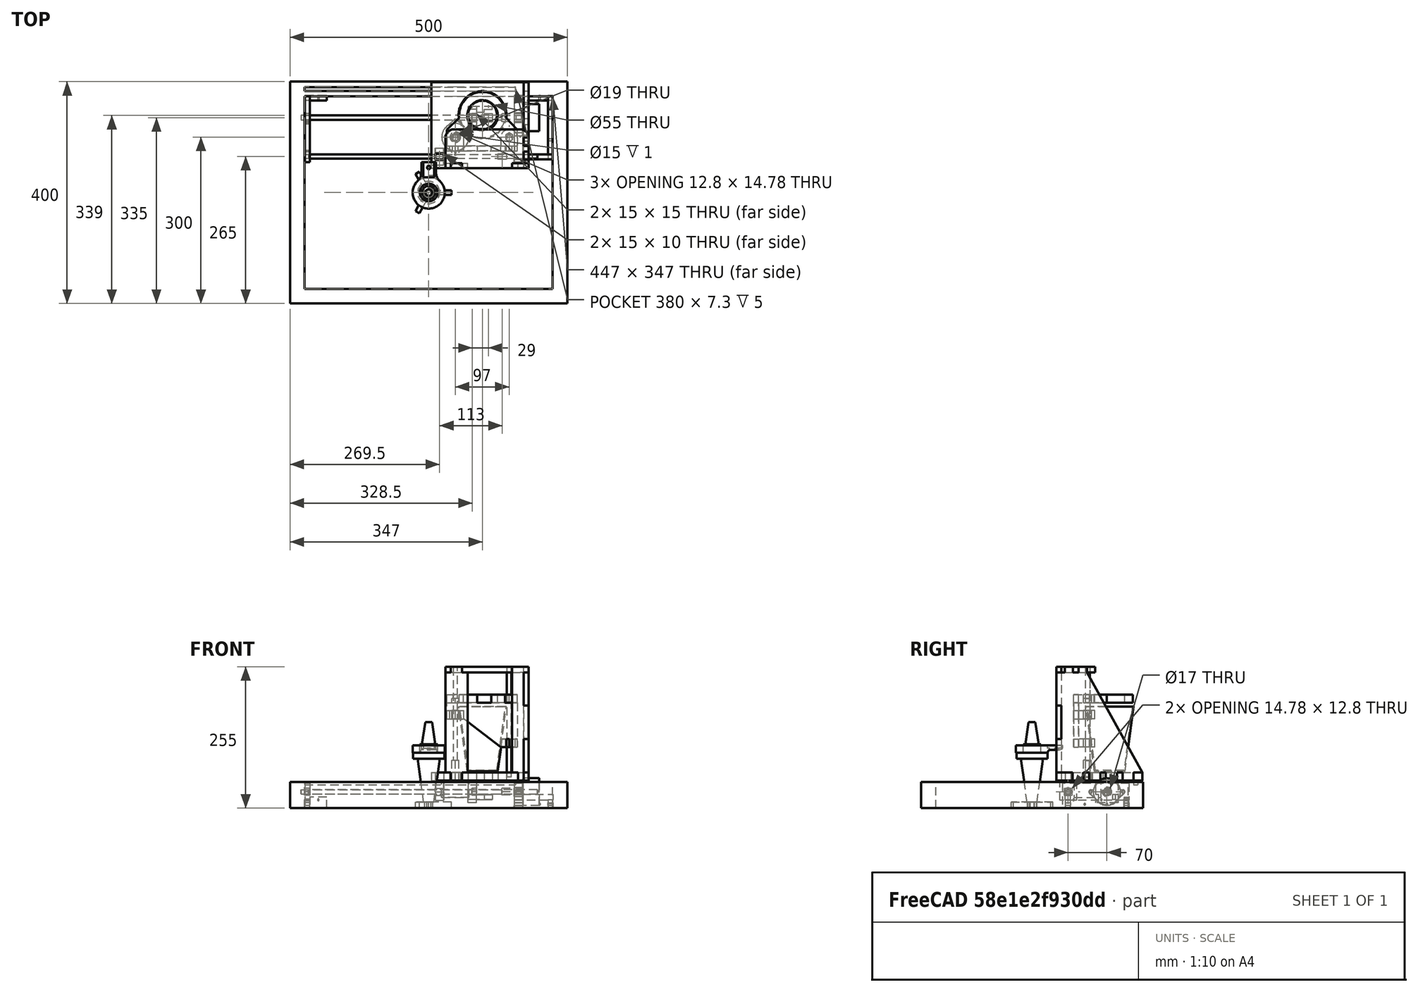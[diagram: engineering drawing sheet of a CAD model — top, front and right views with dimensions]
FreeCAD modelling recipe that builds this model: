
FCSTD DOCUMENT  (FreeCAD 0.19R19093 (Git))
Label: CocktailAutomat-neu
License: All rights reserved
LicenseURL: http://en.wikipedia.org/wiki/All_rights_reserved
objects: Sketcher::SketchObject×41, PartDesign::Body×32, PartDesign::Pad×32, PartDesign::ShapeBinder×14, PartDesign::Plane×7, PartDesign::CoordinateSystem×7, App::Part×7, TechDraw::DrawViewDimension×7, PartDesign::Pocket×6, PartDesign::Revolution×3, PartDesign::FeatureBase×3, TechDraw::DrawProjGroupItem×3, App::DocumentObjectGroup×2, PartDesign::Hole×1, TechDraw::DrawSVGTemplate×1, TechDraw::DrawProjGroup×1, App::FeaturePython×1, TechDraw::DrawPage×1
note: 188 computed .brp shape members not serialized (recipe doc carries the construction recipe); baked Part::Feature solids carry a one-line shape summary decoded from their .brp

FEATURE [Sketcher::SketchObject] Sketch
  MapMode = 5
  Placement = pos=(0,0,0) rot=(0.57735,0.57735,0.57735;2.0944rad)
  Support = -> [YZ_Plane]
  sketch-geometry (6):
    g0: LineSegment StartX=0 StartY=0 StartZ=0 EndX=27.5 EndY=0 EndZ=0
    g1: LineSegment StartX=27.5 StartY=0 StartZ=0 EndX=43 EndY=117 EndZ=0
    g2: LineSegment StartX=43 StartY=117 StartZ=0 EndX=40.9825 EndY=117 EndZ=0
    g3: LineSegment StartX=40.9825 StartY=117 StartZ=0 EndX=25.7475 EndY=2 EndZ=0
    g4: LineSegment StartX=25.7475 StartY=2 StartZ=0 EndX=0 EndY=2 EndZ=0
    g5: LineSegment StartX=0 StartY=2 StartZ=0 EndX=0 EndY=0 EndZ=0
  constraints (17):
    c: Coincident(g-1,g0)
    c: PointOnObject(g0,g-1)
    c: Coincident(g0,g1)
    c: Coincident(g1,g2)
    c: Coincident(g2,g3)
    c: Coincident(g3,g4)
    c: PointOnObject(g4,g-2)
    c: Horizontal(g4)
    c: Coincident(g4,g5)
    c: Coincident(g5,g0)
    c: DistanceX(g0,g0) = 27.5
    c: Parallel(g3,g1)
    c: DistanceY(g5,g5) = 2
    c: Horizontal(g2)
    c: Distance(g1,g-1) = 117
    c: Distance(g1,g-2) = 43
    c: Distance(g2,g1) = 2
FEATURE [PartDesign::Revolution] Revolution
  Angle = 360
  Axis = (-3e-16,3e-16,1)
  Base = (0,0,0)
  Placement = pos=(0,0,0) rot=(0.57735,0.57735,0.57735;2.0944rad)
  Profile = -> Sketch
  ReferenceAxis = -> Z_Axis
  Reversed = true
FEATURE [PartDesign::Body] Body  label="Glas"
  Group = -> [Sketch,Revolution]
  Origin = -> Origin
  Placement = pos=(97,140,66) rot=(0,0,1;0rad)
  Tip = -> Revolution
FEATURE [Sketcher::SketchObject] Sketch001
  MapMode = 5
  Support = -> [XY_Plane001]
  sketch-geometry (16):
    g0: Circle CenterX=0 CenterY=0 CenterZ=0 NormalX=0 NormalY=0 NormalZ=1 AngleXU=0 Radius=3.9
    g1: ArcOfCircle CenterX=0 CenterY=0 CenterZ=0 NormalX=0 NormalY=0 NormalZ=1 AngleXU=0 Radius=8.1 StartAngle=2.61088 EndAngle=3.6723
    g2: LineSegment StartX=7.04344 StartY=4 StartZ=0 EndX=41.0434 EndY=4 EndZ=0
    g3: LineSegment StartX=41.0434 StartY=4 StartZ=0 EndX=41.0434 EndY=-4 EndZ=0
    g4: LineSegment StartX=41.0434 StartY=-4 StartZ=0 EndX=7.04344 EndY=-4 EndZ=0
    g5: LineSegment StartX=-6.98582 StartY=4.0998 StartZ=0 EndX=-23.9858 EndY=33.5447 EndZ=0
    g6: LineSegment StartX=-23.9858 StartY=33.5447 StartZ=0 EndX=-17.0576 EndY=37.5447 EndZ=0
    g7: LineSegment StartX=-17.0576 StartY=37.5447 StartZ=0 EndX=-0.0576167 EndY=8.0998 EndZ=0
    g8: LineSegment StartX=-6.98582 StartY=-4.0998 StartZ=0 EndX=-23.9858 EndY=-33.5447 EndZ=0
    g9: LineSegment StartX=-23.9858 StartY=-33.5447 StartZ=0 EndX=-17.0576 EndY=-37.5447 EndZ=0
    g10: LineSegment StartX=-17.0576 StartY=-37.5447 StartZ=0 EndX=-0.0576167 EndY=-8.0998 EndZ=0
    g11: LineSegment [constr] StartX=0 StartY=0 StartZ=0 EndX=41.0434 EndY=0 EndZ=0
    g12: LineSegment [constr] StartX=0 StartY=0 StartZ=0 EndX=-20.5217 EndY=35.5447 EndZ=0
    g13: LineSegment [constr] StartX=0 StartY=0 StartZ=0 EndX=-20.5217 EndY=-35.5447 EndZ=0
    g14: ArcOfCircle CenterX=0 CenterY=0 CenterZ=0 NormalX=0 NormalY=0 NormalZ=1 AngleXU=0 Radius=8.1 StartAngle=0.516486 EndAngle=1.57791
    g15: ArcOfCircle CenterX=0 CenterY=0 CenterZ=0 NormalX=0 NormalY=0 NormalZ=1 AngleXU=0 Radius=8.1 StartAngle=4.70528 EndAngle=5.7667
  constraints (44):
    c: Coincident(g1,g0)
    c: Coincident(g2,g3)
    c: Coincident(g3,g4)
    c: Coincident(g5,g6)
    c: Coincident(g6,g7)
    c: Coincident(g8,g9)
    c: Coincident(g9,g10)
    c: Coincident(g11,g0)
    c: PointOnObject(g11,g3)
    c: Coincident(g12,g0)
    c: PointOnObject(g12,g6)
    c: Coincident(g13,g0)
    c: PointOnObject(g13,g9)
    c: Diameter(g0) = 7.8
    c: Diameter(g1) = 16.2
    c: Angle(g11,g12) = 2.0944
    c: Angle(g13,g11) = 2.0944
    c: Symmetric(g5,g6,g12)
    c: Distance(g6) = 8
    c: Symmetric(g8,g9,g13)
    c: Parallel(g5,g7)
    c: Parallel(g5,g12)
    c: Parallel(g8,g13)
    c: Parallel(g13,g10)
    c: Distance(g9) = 8
    c: Symmetric(g3,g2,g11)
    c: Parallel(g2,g11)
    c: Parallel(g11,g4)
    c: Distance(g3) = 8
    c: Coincident(g-1,g0)
    c: Horizontal(g11)
    c: Coincident(g1,g5)
    c: Coincident(g14,g7)
    c: Equal(g1,g14)
    c: Coincident(g14,g2)
    c: Coincident(g1,g14)
    c: Coincident(g15,g4)
    c: Equal(g1,g15)
    c: Coincident(g15,g10)
    c: Coincident(g1,g15)
    c: Coincident(g1,g8)
    c: DistanceX(g2,g2) = 34
    c: Distance(g7) = 34
    c: Distance(g8) = 34
FEATURE [PartDesign::Pad] Pad
  Length = 11
  Length2 = 100
  Profile = -> Sketch001
  Type = 0
FEATURE [PartDesign::Body] Body001  label="Dosierer-unten"
  Group = -> [Sketch001,Pad]
  Origin = -> Origin001
  Tip = -> Pad
FEATURE [Sketcher::SketchObject] Sketch002
  MapMode = 5
  Placement = pos=(0,0,0) rot=(0.57735,0.57735,0.57735;2.0944rad)
  Support = -> [YZ_Plane002]
  sketch-geometry (14):
    g0: LineSegment StartX=0 StartY=11 StartZ=0 EndX=9 EndY=11 EndZ=0
    g1: LineSegment StartX=9 StartY=11 StartZ=0 EndX=20 EndY=89 EndZ=0
    g2: LineSegment StartX=20 StartY=89 StartZ=0 EndX=28 EndY=89 EndZ=0
    g3: LineSegment StartX=28 StartY=89 StartZ=0 EndX=28 EndY=100 EndZ=0
    g4: LineSegment StartX=16 StartY=100 StartZ=0 EndX=16 EndY=115 EndZ=0
    g5: LineSegment StartX=16 StartY=115 StartZ=0 EndX=12 EndY=115 EndZ=0
    g6: LineSegment StartX=12 StartY=115 StartZ=0 EndX=6 EndY=155 EndZ=0
    g7: LineSegment StartX=6 StartY=155 StartZ=0 EndX=0 EndY=155 EndZ=0
    g8: LineSegment StartX=0 StartY=155 StartZ=0 EndX=0 EndY=11 EndZ=0
    g9: LineSegment [constr] StartX=6 StartY=155 StartZ=0 EndX=12 EndY=155 EndZ=0
    g10: LineSegment [constr] StartX=12 StartY=115 StartZ=0 EndX=12 EndY=155 EndZ=0
    g11: LineSegment [constr] StartX=9 StartY=11 StartZ=0 EndX=20 EndY=11 EndZ=0
    g12: LineSegment [constr] StartX=20 StartY=89 StartZ=0 EndX=20 EndY=11 EndZ=0
    g13: LineSegment StartX=16 StartY=100 StartZ=0 EndX=28 EndY=100 EndZ=0
  constraints (42):
    c: PointOnObject(g0,g-2)
    c: Horizontal(g0)
    c: Coincident(g1,g2)
    c: Coincident(g2,g3)
    c: Vertical(g3)
    c: Vertical(g4)
    c: Coincident(g4,g5)
    c: Coincident(g5,g6)
    c: Coincident(g6,g7)
    c: PointOnObject(g7,g-2)
    c: Coincident(g8,g7)
    c: Coincident(g8,g0)
    c: Distance(g0) = 9
    c: Coincident(g1,g0)
    c: Distance(g1,g8) = 20
    c: Distance(g3) = 11
    c: Perpendicular(g2,g3)
    c: Distance(g2) = 8
    c: Distance(g4) = 15
    c: Distance(g5) = 4
    c: Perpendicular(g4,g5)
    c: Distance(g7) = 6
    c: Horizontal(g7)
    c: Coincident(g9,g6)
    c: Horizontal(g9)
    c: Coincident(g10,g5)
    c: Coincident(g10,g9)
    c: Vertical(g10)
    c: Distance(g10) = 40
    c: Coincident(g11,g0)
    c: Coincident(g12,g1)
    c: Coincident(g12,g11)
    c: Vertical(g12)
    c: Horizontal(g11)
    c: Distance(g12) = 78
    c: Distance(g0,g-1) = 11
    c: Coincident(g13,g4)
    c: Coincident(g13,g3)
    c: Horizontal(g13)
    c: Distance(g13) = 12
    c: Distance(g3,g-1) = 100
    c: Distance(g3,g8) = 28
FEATURE [PartDesign::Revolution] Revolution001
  Angle = 360
  Axis = (-3e-16,3e-16,1)
  Base = (0,0,0)
  Placement = pos=(0,0,0) rot=(0.57735,0.57735,0.57735;2.0944rad)
  Profile = -> Sketch002
  ReferenceAxis = -> Z_Axis002
  Reversed = true
FEATURE [PartDesign::Body] Body002  label="Dosierer - mitte"
  Group = -> [Sketch002,Revolution001]
  Origin = -> Origin002
  Tip = -> Revolution001
FEATURE [PartDesign::ShapeBinder] CopyRevolution001
  Placement = pos=(0,0,0) rot=(0.57735,0.57735,0.57735;2.0944rad)
  TraceSupport = false
FEATURE [PartDesign::Plane] DatumPlane
  Length = 97.9587
  MapMode = 5
  Placement = pos=(-5.6e-14,3.3e-14,100) rot=(0,0,-1;1.5708rad)
  ResizeMode = 0
  Support = -> [CopyRevolution001]
  Width = 71.948
FEATURE [Sketcher::SketchObject] Sketch003
  MapMode = 5
  Placement = pos=(-5.6e-14,3.3e-14,100) rot=(0,0,-1;1.5708rad)
  Support = -> [CopyRevolution001]
  sketch-geometry (6):
    g0: LineSegment StartX=-55 StartY=-13 StartZ=0 EndX=-55 EndY=13 EndZ=0
    g1: LineSegment StartX=-55 StartY=13 StartZ=0 EndX=-37 EndY=13 EndZ=0
    g2: LineSegment StartX=-37 StartY=-13 StartZ=0 EndX=-55 EndY=-13 EndZ=0
    g3: ArcOfCircle CenterX=0 CenterY=0 CenterZ=0 NormalX=0 NormalY=0 NormalZ=1 AngleXU=0 Radius=29 StartAngle=3.89609 EndAngle=8.67028
    g4: ArcOfCircle CenterX=-37 CenterY=34.7813 CenterZ=0 NormalX=0 NormalY=0 NormalZ=1 AngleXU=0 Radius=21.7813 StartAngle=4.71239 EndAngle=5.52869
    g5: ArcOfCircle CenterX=-37 CenterY=-34.7812 CenterZ=0 NormalX=0 NormalY=0 NormalZ=1 AngleXU=0 Radius=21.7812 StartAngle=0.754498 EndAngle=1.5708
  constraints (15):
    c: Coincident(g0,g1)
    c: Horizontal(g1)
    c: Coincident(g2,g0)
    c: Symmetric(g0,g0,g-1)
    c: Distance(g0) = 26
    c: Coincident(g3,g-1)
    c: Diameter(g3) = 58
    c: Horizontal(g2)
    c: Distance(g3,g0) = 55
    c: Tangent(g1,g4) = -1.5708
    c: Tangent(g3,g4) = 1.5708
    c: Tangent(g2,g5) = -1.5708
    c: Tangent(g3,g5) = 1.5708
    c: Distance(g1) = 18
    c: Equal(g2,g1)
FEATURE [PartDesign::Pad] Pad001
  Length = 13
  Length2 = 100
  Placement = pos=(0,0,0) rot=(0.57735,0.57735,0.57735;2.0944rad)
  Profile = -> Sketch003
  Type = 0
FEATURE [Sketcher::SketchObject] Sketch004
  ExternalGeometry = -> [Pad001]
  MapMode = 5
  Placement = pos=(-4.41e-14,3.96e-14,113) rot=(0,0,-1;1.5708rad)
  Support = -> [Pad001]
  sketch-geometry (4):
    g0: LineSegment StartX=-55 StartY=10 StartZ=0 EndX=-27.5 EndY=10 EndZ=0
    g1: LineSegment StartX=-27.5 StartY=10 StartZ=0 EndX=-27.5 EndY=-10 EndZ=0
    g2: LineSegment StartX=-27.5 StartY=-10 StartZ=0 EndX=-55 EndY=-10 EndZ=0
    g3: LineSegment StartX=-55 StartY=-10 StartZ=0 EndX=-55 EndY=10 EndZ=0
  constraints (11):
    c: Coincident(g0,g1)
    c: Coincident(g1,g2)
    c: Coincident(g2,g3)
    c: Coincident(g3,g0)
    c: Horizontal(g0)
    c: Horizontal(g2)
    c: Vertical(g1)
    c: PointOnObject(g0,g-3)
    c: Symmetric(g2,g0,g-1)
    c: Distance(g3) = 20
    c: Distance(g0) = 27.5
FEATURE [PartDesign::Pocket] Pocket
  BaseFeature = -> Pad001
  Length = 4.5
  Length2 = 100
  Placement = pos=(0,0,0) rot=(0.57735,0.57735,0.57735;2.0944rad)
  Profile = -> Sketch004
  Type = 0
FEATURE [Sketcher::SketchObject] Sketch005
  ExternalGeometry = -> [Pocket]
  MapMode = 5
  Placement = pos=(-7.7e-14,5.64e-14,108.5) rot=(0,0,-1;1.5708rad)
  Support = -> [Pocket]
  sketch-geometry (1):
    g0: Circle CenterX=-45.05 CenterY=0 CenterZ=0 NormalX=0 NormalY=0 NormalZ=1 AngleXU=0 Radius=2.45
  constraints (3):
    c: PointOnObject(g0,g-1)
    c: Diameter(g0) = 4.9
    c: Distance(g0,g-3) = 9.95
FEATURE [PartDesign::Hole] Hole
  BaseFeature = -> Pocket
  Depth = 25
  DepthType = 0
  Diameter = 6
  DrillPoint = 1
  DrillPointAngle = 118
  HoleCutCountersinkAngle = 90
  HoleCutDepth = 0
  HoleCutDiameter = 0
  HoleCutType = 0
  ModelActualThread = false
  Placement = pos=(0,0,0) rot=(0.57735,0.57735,0.57735;2.0944rad)
  Profile = -> Sketch005
  Tapered = false
  TaperedAngle = 90
  ThreadAngle = 0
  ThreadClass = 0
  ThreadCutOffInner = 0
  ThreadCutOffOuter = 0
  ThreadDirection = 0
  ThreadFit = 0
  ThreadPitch = 0
  ThreadSize = 0
  ThreadType = 0
  Threaded = false
FEATURE [Sketcher::SketchObject] Sketch006
  ExternalGeometry = -> [Hole]
  MapMode = 5
  Placement = pos=(13,2.9e-15,1.01e-14) rot=(0.57735,0.57735,0.57735;2.0944rad)
  Support = -> [Hole]
  sketch-geometry (5):
    g0: LineSegment StartX=55 StartY=107 StartZ=0 EndX=49 EndY=105 EndZ=0
    g1: LineSegment StartX=49 StartY=105 StartZ=0 EndX=30.5 EndY=105 EndZ=0
    g2: LineSegment StartX=30.5 StartY=105 StartZ=0 EndX=27.5 EndY=100 EndZ=0
    g3: LineSegment StartX=27.5 StartY=100 StartZ=0 EndX=55 EndY=100 EndZ=0
    g4: LineSegment StartX=55 StartY=100 StartZ=0 EndX=55 EndY=107 EndZ=0
  constraints (14):
    c: Coincident(g0,g1)
    c: Horizontal(g1)
    c: Coincident(g1,g2)
    c: Coincident(g2,g3)
    c: Horizontal(g3)
    c: Coincident(g3,g4)
    c: Coincident(g4,g0)
    c: Vertical(g4)
    c: Coincident(g3,g-3)
    c: Distance(g0,g-3) = 6
    c: DistanceY(g1,g-3) = 8
    c: Distance(g3) = 27.5
    c: Distance(g1) = 18.5
    c: Distance(g0,g4) = 6
FEATURE [PartDesign::Pocket] Pocket001
  BaseFeature = -> Hole
  Length = 27
  Length2 = 100
  Midplane = true
  Placement = pos=(0,0,0) rot=(0.57735,0.57735,0.57735;2.0944rad)
  Profile = -> Sketch006
  Type = 1
FEATURE [PartDesign::Body] Body003  label="Dosierer halterung"
  Group = -> [DatumPlane,CopyRevolution001,Sketch003,Pad001,Sketch004,Pocket,Sketch005,Hole,Sketch006,Pocket001]
  Origin = -> Origin003
  Tip = -> Pocket001
FEATURE [Sketcher::SketchObject] Sketch007
  MapMode = 5
  Support = -> [XY_Plane004]
  sketch-geometry (8):
    g0: LineSegment StartX=-223.5 StartY=173.5 StartZ=0 EndX=223.5 EndY=173.5 EndZ=0
    g1: LineSegment StartX=223.5 StartY=173.5 StartZ=0 EndX=223.5 EndY=-173.5 EndZ=0
    g2: LineSegment StartX=223.5 StartY=-173.5 StartZ=0 EndX=-223.5 EndY=-173.5 EndZ=0
    g3: LineSegment StartX=-223.5 StartY=-173.5 StartZ=0 EndX=-223.5 EndY=173.5 EndZ=0
    g4: LineSegment StartX=-250 StartY=200 StartZ=0 EndX=250 EndY=200 EndZ=0
    g5: LineSegment StartX=250 StartY=200 StartZ=0 EndX=250 EndY=-200 EndZ=0
    g6: LineSegment StartX=250 StartY=-200 StartZ=0 EndX=-250 EndY=-200 EndZ=0
    g7: LineSegment StartX=-250 StartY=-200 StartZ=0 EndX=-250 EndY=200 EndZ=0
  constraints (20):
    c: Coincident(g0,g1)
    c: Coincident(g1,g2)
    c: Coincident(g2,g3)
    c: Coincident(g3,g0)
    c: Horizontal(g2)
    c: Vertical(g3)
    c: Coincident(g4,g5)
    c: Coincident(g5,g6)
    c: Coincident(g6,g7)
    c: Coincident(g7,g4)
    c: Horizontal(g6)
    c: Vertical(g7)
    c: DistanceY(g5,g5) = 400
    c: DistanceX(g4,g4) = 500
    c: Distance(g1,g5) = 26.5
    c: Symmetric(g4,g4,g-2)
    c: Symmetric(g0,g0,g-2)
    c: Symmetric(g4,g5,g-1)
    c: Distance(g1,g6) = 26.5
    c: Symmetric(g0,g1,g-1)
FEATURE [PartDesign::Pad] Pad002
  Length = 47
  Length2 = 100
  Profile = -> Sketch007
  Type = 0
FEATURE [Sketcher::SketchObject] Sketch008
  ExternalGeometry = -> [Pad002]
  MapMode = 5
  Placement = pos=(-223.5,0,0) rot=(0.57735,0.57735,0.57735;2.0944rad)
  Support = -> [Pad002]
  sketch-geometry (8):
    g0: LineSegment StartX=183.1 StartY=42 StartZ=0 EndX=183.1 EndY=47 EndZ=0
    g1: LineSegment StartX=183.1 StartY=47 StartZ=0 EndX=190.4 EndY=47 EndZ=0
    g2: LineSegment StartX=190.4 StartY=47 StartZ=0 EndX=190.4 EndY=42 EndZ=0
    g3: LineSegment StartX=190.4 StartY=42 StartZ=0 EndX=189.4 EndY=42 EndZ=0
    g4: LineSegment StartX=189.4 StartY=42 StartZ=0 EndX=189.4 EndY=46 EndZ=0
    g5: LineSegment StartX=189.4 StartY=46 StartZ=0 EndX=184.1 EndY=46 EndZ=0
    g6: LineSegment StartX=184.1 StartY=46 StartZ=0 EndX=184.1 EndY=42 EndZ=0
    g7: LineSegment StartX=184.1 StartY=42 StartZ=0 EndX=183.1 EndY=42 EndZ=0
  constraints (24):
    c: Vertical(g0)
    c: Coincident(g0,g1)
    c: Coincident(g1,g2)
    c: Coincident(g2,g3)
    c: Coincident(g3,g4)
    c: Coincident(g4,g5)
    c: Coincident(g5,g6)
    c: Coincident(g6,g7)
    c: Coincident(g7,g0)
    c: Vertical(g2)
    c: Horizontal(g1)
    c: Horizontal(g5)
    c: Horizontal(g7)
    c: Horizontal(g3)
    c: Vertical(g6)
    c: Vertical(g4)
    c: DistanceX(g1,g1) = 7.3
    c: Distance(g4,g2) = 1
    c: DistanceY(g0,g0) = 5
    c: Distance(g5,g0) = 1
    c: DistanceY(g2,g2) = 5
    c: Distance(g5,g1) = 1
    c: DistanceX(g-3,g0) = 9.6
    c: DistanceY(g0,g-3) = 0
FEATURE [PartDesign::Pad] Pad003
  BaseFeature = -> Pad002
  Length = 380
  Length2 = 100
  Profile = -> Sketch008
  Type = 0
FEATURE [PartDesign::Pocket] Pocket002
  BaseFeature = -> Pad003
  Length = 5
  Length2 = 100
  Profile = -> Pad003 [Face11]
  Type = 0
FEATURE [PartDesign::Body] Body004  label="Grundgestell"
  Group = -> [Sketch007,Pad002,Sketch008,Pad003,Pocket002]
  Origin = -> Origin004
  Tip = -> Pocket002
FEATURE [Sketcher::SketchObject] Sketch009
  MapMode = 5
  Placement = pos=(0,0,0) rot=(0.57735,0.57735,0.57735;2.0944rad)
  Support = -> [YZ_Plane005]
  sketch-geometry (1):
    g0: Circle CenterX=0 CenterY=0 CenterZ=0 NormalX=0 NormalY=0 NormalZ=1 AngleXU=0 Radius=24.5
  constraints (2):
    c: Diameter(g0) = 49
    c: Coincident(g0,g-1)
FEATURE [PartDesign::Pad] Pad004
  Length = 29
  Length2 = 100
  Placement = pos=(0,0,0) rot=(0.57735,0.57735,0.57735;2.0944rad)
  Profile = -> Sketch009
  Type = 0
FEATURE [Sketcher::SketchObject] Sketch010
  MapMode = 5
  Support = -> [XY_Plane005]
  sketch-geometry (8):
    g0: LineSegment StartX=-2 StartY=5 StartZ=0 EndX=-2 EndY=2 EndZ=0
    g1: LineSegment StartX=-2 StartY=2 StartZ=0 EndX=-3 EndY=2 EndZ=0
    g2: LineSegment StartX=-3 StartY=2 StartZ=0 EndX=-3 EndY=3.8 EndZ=0
    g3: LineSegment StartX=-3 StartY=3.8 StartZ=0 EndX=-13 EndY=3.8 EndZ=0
    g4: LineSegment StartX=-13 StartY=3.8 StartZ=0 EndX=-13 EndY=0 EndZ=0
    g5: LineSegment StartX=-13 StartY=0 StartZ=0 EndX=0 EndY=0 EndZ=0
    g6: LineSegment StartX=0 StartY=0 StartZ=0 EndX=0 EndY=5 EndZ=0
    g7: LineSegment StartX=-2 StartY=5 StartZ=0 EndX=0 EndY=5 EndZ=0
  constraints (23):
    c: Coincident(g0,g1)
    c: Coincident(g1,g2)
    c: Coincident(g2,g3)
    c: Horizontal(g3)
    c: Coincident(g3,g4)
    c: PointOnObject(g4,g-1)
    c: Vertical(g4)
    c: Coincident(g4,g5)
    c: Coincident(g5,g-1)
    c: Coincident(g5,g6)
    c: Vertical(g6)
    c: Coincident(g7,g0)
    c: Coincident(g7,g6)
    c: Horizontal(g7)
    c: Vertical(g0)
    c: Horizontal(g1)
    c: Vertical(g2)
    c: DistanceY(g6,g6) = 5
    c: DistanceX(g7,g7) = 2
    c: DistanceY(g0,g0) = 3
    c: DistanceX(g1,g1) = 1
    c: DistanceX(g3,g3) = 10
    c: DistanceY(g4,g4) = 3.8
FEATURE [PartDesign::Revolution] Revolution002
  Angle = 360
  Axis = (1,0,0)
  Base = (0,0,0)
  BaseFeature = -> Pad004
  Placement = pos=(0,0,0) rot=(0.57735,0.57735,0.57735;2.0944rad)
  Profile = -> Sketch010
  ReferenceAxis = -> X_Axis005
FEATURE [Sketcher::SketchObject] Sketch011
  MapMode = 5
  Placement = pos=(0,0,0) rot=(0.57735,0.57735,0.57735;2.0944rad)
  Support = -> [YZ_Plane005]
  sketch-geometry (11):
    g0: Circle [constr] CenterX=0 CenterY=0 CenterZ=0 NormalX=0 NormalY=0 NormalZ=1 AngleXU=0 Radius=23.25
    g1: ArcOfCircle CenterX=-29 CenterY=0 CenterZ=0 NormalX=0 NormalY=0 NormalZ=1 AngleXU=0 Radius=3.5 StartAngle=1.5708 EndAngle=3.96321
    g2: ArcOfCircle CenterX=29 CenterY=0 CenterZ=0 NormalX=0 NormalY=0 NormalZ=1 AngleXU=0 Radius=3.5 StartAngle=5.46156 EndAngle=7.85398
    g3: LineSegment StartX=31.3836 StartY=-2.56288 StartZ=0 EndX=15.8341 EndY=-17.0248 EndZ=0
    g4: LineSegment StartX=22.985 StartY=3.5 StartZ=0 EndX=29 EndY=3.5 EndZ=0
    g5: LineSegment StartX=-31.3836 StartY=-2.56288 StartZ=0 EndX=-15.834 EndY=-17.0248 EndZ=0
    g6: LineSegment StartX=-29 StartY=3.5 StartZ=0 EndX=-22.985 EndY=3.5 EndZ=0
    g7: ArcOfCircle CenterX=0 CenterY=0 CenterZ=0 NormalX=0 NormalY=0 NormalZ=1 AngleXU=0 Radius=23.25 StartAngle=0.151112 EndAngle=2.99048
    g8: ArcOfCircle CenterX=0 CenterY=0 CenterZ=0 NormalX=0 NormalY=0 NormalZ=1 AngleXU=0 Radius=23.25 StartAngle=3.96321 EndAngle=5.46156
    g9: Circle CenterX=-29 CenterY=0 CenterZ=0 NormalX=0 NormalY=0 NormalZ=1 AngleXU=0 Radius=2.5
    g10: Circle CenterX=29 CenterY=0 CenterZ=0 NormalX=0 NormalY=0 NormalZ=1 AngleXU=0 Radius=2.5
  constraints (30):
    c: Diameter(g0) = 46.5
    c: PointOnObject(g1,g-1)
    c: Symmetric(g1,g2,g-2)
    c: Equal(g2,g1)
    c: Diameter(g2) = 7
    c: DistanceX(g-2,g2) = 29
    c: Coincident(g0,g-1)
    c: Tangent(g3,g0)
    c: Tangent(g3,g2)
    c: PointOnObject(g4,g0)
    c: Horizontal(g4)
    c: PointOnObject(g5,g0)
    c: Horizontal(g6)
    c: Tangent(g6,g1)
    c: Tangent(g5,g0)
    c: Coincident(g7,g-1)
    c: Coincident(g7,g4)
    c: Coincident(g7,g6)
    c: Coincident(g8,g7)
    c: Coincident(g8,g5)
    c: Coincident(g8,g3)
    c: Tangent(g4,g2)
    c: Coincident(g1,g6)
    c: Coincident(g2,g3)
    c: Coincident(g2,g4)
    c: Tangent(g1,g5) = -1.5708
    c: Coincident(g9,g1)
    c: Coincident(g10,g2)
    c: Equal(g10,g9)
    c: Diameter(g9) = 5
FEATURE [PartDesign::Pad] Pad005
  BaseFeature = -> Revolution002
  Length = 0.8
  Length2 = 100
  Placement = pos=(0,0,0) rot=(0.57735,0.57735,0.57735;2.0944rad)
  Profile = -> Sketch011
  Reversed = true
  Type = 0
FEATURE [PartDesign::Body] Body005  label="Motor"
  Group = -> [Sketch009,Pad004,Sketch010,Revolution002,Sketch011,Pad005]
  Origin = -> Origin005
  Placement = pos=(170,135,29.5) rot=(0,0,1;0rad)
  Tip = -> Pad005
FEATURE [Sketcher::SketchObject] Sketch012
  MapMode = 5
  Placement = pos=(0,0,0) rot=(0.57735,0.57735,0.57735;2.0944rad)
  Support = -> [YZ_Plane007]
  sketch-geometry (1):
    g0: Circle CenterX=0 CenterY=0 CenterZ=0 NormalX=0 NormalY=0 NormalZ=1 AngleXU=0 Radius=4
  constraints (2):
    c: Coincident(g0,g-1)
    c: Diameter(g0) = 8
FEATURE [PartDesign::Pad] Pad006
  Length = 413
  Length2 = 100
  Placement = pos=(0,0,0) rot=(0.57735,0.57735,0.57735;2.0944rad)
  Profile = -> Sketch012
  Type = 0
FEATURE [PartDesign::Body] Body007  label="runde Stange"
  Group = -> [Sketch012,Pad006]
  Origin = -> Origin007
  Placement = pos=(-217,65,29) rot=(0,0,1;0rad)
  Tip = -> Pad006
FEATURE [Sketcher::SketchObject] Sketch033
  MapMode = 5
  Support = -> [XY_Plane012]
  sketch-geometry (1):
    g0: Circle CenterX=0 CenterY=0 CenterZ=0 NormalX=0 NormalY=0 NormalZ=1 AngleXU=0 Radius=24.5
  constraints (2):
    c: Coincident(g0,g-1)
    c: Diameter(g0) = 49
FEATURE [PartDesign::Pad] Pad011
  Length = 29
  Length2 = 100
  Profile = -> Sketch033
  Reversed = true
  Type = 0
FEATURE [Sketcher::SketchObject] Sketch034
  MapMode = 5
  Support = -> [Pad011]
  sketch-geometry (14):
    g0: Circle CenterX=0 CenterY=0 CenterZ=0 NormalX=0 NormalY=0 NormalZ=1 AngleXU=0 Radius=7.5
    g1: Circle CenterX=-28.2 CenterY=0 CenterZ=0 NormalX=0 NormalY=0 NormalZ=1 AngleXU=0 Radius=1.5
    g2: Circle CenterX=28.2 CenterY=0 CenterZ=0 NormalX=0 NormalY=0 NormalZ=1 AngleXU=0 Radius=1.5
    g3: Circle [constr] CenterX=0 CenterY=0 CenterZ=0 NormalX=0 NormalY=0 NormalZ=1 AngleXU=0 Radius=24.5
    g4: Circle [constr] CenterX=-28.2 CenterY=0 CenterZ=0 NormalX=0 NormalY=0 NormalZ=1 AngleXU=0 Radius=4
    g5: Circle [constr] CenterX=28.2 CenterY=0 CenterZ=0 NormalX=0 NormalY=0 NormalZ=1 AngleXU=0 Radius=4
    g6: LineSegment StartX=-31.1078 StartY=2.74676 StartZ=0 EndX=-17.8103 EndY=16.8239 EndZ=0
    g7: LineSegment StartX=17.8103 StartY=16.8239 StartZ=0 EndX=31.1078 EndY=2.74676 EndZ=0
    g8: LineSegment StartX=-31.1078 StartY=-2.74676 StartZ=0 EndX=-17.8103 EndY=-16.8239 EndZ=0
    g9: LineSegment StartX=17.8103 StartY=-16.8239 StartZ=0 EndX=31.1078 EndY=-2.74676 EndZ=0
    g10: ArcOfCircle CenterX=-28.2 CenterY=0 CenterZ=0 NormalX=0 NormalY=0 NormalZ=1 AngleXU=0 Radius=4 StartAngle=2.38467 EndAngle=3.89852
    g11: ArcOfCircle CenterX=0 CenterY=0 CenterZ=0 NormalX=0 NormalY=0 NormalZ=1 AngleXU=0 Radius=24.5 StartAngle=3.89852 EndAngle=5.52626
    g12: ArcOfCircle CenterX=0 CenterY=0 CenterZ=0 NormalX=0 NormalY=0 NormalZ=1 AngleXU=0 Radius=24.5 StartAngle=0.756926 EndAngle=2.38467
    g13: ArcOfCircle CenterX=28.2 CenterY=0 CenterZ=0 NormalX=0 NormalY=0 NormalZ=1 AngleXU=0 Radius=4 StartAngle=5.52626 EndAngle=7.04011
  constraints (34):
    c: Coincident(g0,g-1)
    c: Diameter(g0) = 15
    c: PointOnObject(g2,g-1)
    c: Diameter(g1) = 3
    c: Diameter(g2) = 3
    c: Symmetric(g1,g2,g0)
    c: Distance(g1,g2) = 56.4
    c: Coincident(g3,g0)
    c: Diameter(g3) = 49
    c: Coincident(g4,g1)
    c: Coincident(g5,g2)
    c: Equal(g4,g5)
    c: Radius(g4) = 4
    c: PointOnObject(g6,g4)
    c: PointOnObject(g6,g3)
    c: Tangent(g6,g3)
    c: PointOnObject(g7,g5)
    c: Tangent(g7,g3)
    c: Tangent(g6,g4)
    c: Tangent(g8,g3)
    c: Coincident(g10,g1)
    c: Coincident(g10,g6)
    c: Coincident(g11,g0)
    c: Coincident(g11,g8)
    c: Coincident(g12,g0)
    c: Coincident(g12,g7)
    c: Coincident(g12,g6)
    c: Coincident(g13,g2)
    c: Tangent(g10,g8) = -1.5708
    c: Coincident(g7,g13)
    c: Tangent(g7,g13)
    c: Tangent(g13,g9) = -1.5708
    c: Tangent(g11,g9) = -1.5708
    c: PointOnObject(g8,g3)
FEATURE [PartDesign::Pad] Pad012
  BaseFeature = -> Pad011
  Length = 1
  Length2 = 100
  Profile = -> Sketch034
  Type = 0
FEATURE [Sketcher::SketchObject] Sketch035
  MapMode = 5
  Support = -> [Pad012]
  sketch-geometry (7):
    g0: LineSegment StartX=3.5 StartY=-6.06218 StartZ=0 EndX=7 EndY=0 EndZ=0
    g1: LineSegment StartX=7 StartY=0 StartZ=0 EndX=3.5 EndY=6.06218 EndZ=0
    g2: LineSegment StartX=3.5 StartY=6.06218 StartZ=0 EndX=-3.5 EndY=6.06218 EndZ=0
    g3: LineSegment StartX=-3.5 StartY=6.06218 StartZ=0 EndX=-7 EndY=-9e-16 EndZ=0
    g4: LineSegment StartX=-7 StartY=-9e-16 StartZ=0 EndX=-3.5 EndY=-6.06218 EndZ=0
    g5: LineSegment StartX=-3.5 StartY=-6.06218 StartZ=0 EndX=3.5 EndY=-6.06218 EndZ=0
    g6: Circle [constr] CenterX=0 CenterY=0 CenterZ=0 NormalX=0 NormalY=0 NormalZ=1 AngleXU=0 Radius=7
  constraints (16):
    c: Coincident(g0,g1)
    c: Coincident(g1,g2)
    c: Coincident(g2,g3)
    c: Coincident(g3,g4)
    c: Coincident(g4,g5)
    c: Coincident(g5,g0)
    c: Equal(g0, g1-g5) x5
    c: PointOnObject(g0,g6)
    c: PointOnObject(g1,g6)
    c: PointOnObject(g2,g6)
    c: PointOnObject(g3,g6)
    c: PointOnObject(g4,g6)
    c: PointOnObject(g5,g6)
    c: Coincident(g6,g-1)
    c: Diameter(g6) = 14
    c: PointOnObject(g0,g-1)
FEATURE [PartDesign::Pad] Pad013
  BaseFeature = -> Pad012
  Length = 38
  Length2 = 100
  Profile = -> Sketch035
  Type = 0
FEATURE [PartDesign::Body] Body012  label="Motor-vertikal"
  Group = -> [Sketch033,Pad011,Sketch034,Pad012,Sketch035,Pad013]
  Origin = -> Origin012
  Placement = pos=(48,100,48.5) rot=(0,0,-1;1.5708rad)
  Tip = -> Pad013
FEATURE [Sketcher::SketchObject] Sketch036
  MapMode = 5
  Placement = pos=(0,0,0) rot=(0.57735,0.57735,0.57735;2.0944rad)
  Support = -> [YZ_Plane013]
  sketch-geometry (1):
    g0: Circle CenterX=0 CenterY=0 CenterZ=0 NormalX=0 NormalY=0 NormalZ=1 AngleXU=0 Radius=4
  constraints (2):
    c: Coincident(g0,g-1)
    c: Diameter(g0) = 8
FEATURE [PartDesign::Pad] Pad014
  Length = 400
  Length2 = 100
  Placement = pos=(0,0,0) rot=(0.57735,0.57735,0.57735;2.0944rad)
  Profile = -> Sketch036
  Reversed = true
  Type = 0
FEATURE [Sketcher::SketchObject] Sketch037
  MapMode = 5
  Placement = pos=(0,0,0) rot=(0.57735,0.57735,0.57735;2.0944rad)
  Support = -> [Pad014]
  sketch-geometry (7):
    g0: LineSegment StartX=3.5 StartY=-6.06218 StartZ=0 EndX=7 EndY=0 EndZ=0
    g1: LineSegment StartX=7 StartY=0 StartZ=0 EndX=3.5 EndY=6.06218 EndZ=0
    g2: LineSegment StartX=3.5 StartY=6.06218 StartZ=0 EndX=-3.5 EndY=6.06218 EndZ=0
    g3: LineSegment StartX=-3.5 StartY=6.06218 StartZ=0 EndX=-7 EndY=-1.8e-15 EndZ=0
    g4: LineSegment StartX=-7 StartY=-1.8e-15 StartZ=0 EndX=-3.5 EndY=-6.06218 EndZ=0
    g5: LineSegment StartX=-3.5 StartY=-6.06218 StartZ=0 EndX=3.5 EndY=-6.06218 EndZ=0
    g6: Circle [constr] CenterX=0 CenterY=0 CenterZ=0 NormalX=0 NormalY=0 NormalZ=1 AngleXU=0 Radius=7
  constraints (16):
    c: Coincident(g0,g1)
    c: Coincident(g1,g2)
    c: Coincident(g2,g3)
    c: Coincident(g3,g4)
    c: Coincident(g4,g5)
    c: Coincident(g5,g0)
    c: Equal(g0, g1-g5) x5
    c: PointOnObject(g0,g6)
    c: PointOnObject(g1,g6)
    c: PointOnObject(g2,g6)
    c: PointOnObject(g3,g6)
    c: PointOnObject(g4,g6)
    c: PointOnObject(g5,g6)
    c: Coincident(g6,g-1)
    c: PointOnObject(g0,g-1)
    c: Diameter(g6) = 14
FEATURE [PartDesign::Pad] Pad015
  BaseFeature = -> Pad014
  Length = 38
  Length2 = 100
  Placement = pos=(0,0,0) rot=(0.57735,0.57735,0.57735;2.0944rad)
  Profile = -> Sketch037
  Reversed = true
  Type = 0
FEATURE [PartDesign::Body] Body013  label="gewindestange-horiz"
  Group = -> [Sketch036,Pad014,Sketch037,Pad015]
  Origin = -> Origin013
  Placement = pos=(170,135,29.5) rot=(0,0,1;0rad)
  Tip = -> Pad015
FEATURE [Sketcher::SketchObject] Sketch038
  MapMode = 5
  Placement = pos=(-0.8,0,0) rot=(0.57735,0.57735,-0.57735;4.18879rad)
  sketch-geometry (24):
    g0: LineSegment StartX=40 StartY=-15 StartZ=0 EndX=-80 EndY=-15 EndZ=0
    g1: LineSegment StartX=-80 StartY=-15 StartZ=0 EndX=-80 EndY=29.5 EndZ=0
    g2: LineSegment StartX=-80 StartY=29.5 StartZ=0 EndX=-75 EndY=29.5 EndZ=0
    g3: LineSegment [constr] StartX=40 StartY=29.5 StartZ=0 EndX=40 EndY=-15 EndZ=0
    g4: Circle CenterX=0 CenterY=0 CenterZ=0 NormalX=0 NormalY=0 NormalZ=1 AngleXU=0 Radius=8.5
    g5: Circle CenterX=-70 CenterY=0 CenterZ=0 NormalX=0 NormalY=0 NormalZ=1 AngleXU=0 Radius=4
    g6: Circle CenterX=29.9 CenterY=0 CenterZ=0 NormalX=0 NormalY=0 NormalZ=1 AngleXU=0 Radius=2.4
    g7: Circle CenterX=-29.9 CenterY=0 CenterZ=0 NormalX=0 NormalY=0 NormalZ=1 AngleXU=0 Radius=2.4
    g8: LineSegment StartX=-66 StartY=29.5 StartZ=0 EndX=-66 EndY=24.5 EndZ=0
    g9: LineSegment StartX=-66 StartY=24.5 StartZ=0 EndX=-75 EndY=24.5 EndZ=0
    g10: LineSegment StartX=-75 StartY=24.5 StartZ=0 EndX=-75 EndY=29.5 EndZ=0
    g11: LineSegment [constr] StartX=-66 StartY=29.5 StartZ=0 EndX=40 EndY=29.5 EndZ=0
    g12: LineSegment StartX=40 StartY=24.5 StartZ=0 EndX=31 EndY=24.5 EndZ=0
    g13: LineSegment StartX=31 StartY=24.5 StartZ=0 EndX=31 EndY=29.5 EndZ=0
    g14: LineSegment StartX=31 StartY=29.5 StartZ=0 EndX=-66 EndY=29.5 EndZ=0
    g15: LineSegment StartX=40 StartY=-15 StartZ=0 EndX=40 EndY=14.5 EndZ=0
    g16: LineSegment StartX=40 StartY=14.5 StartZ=0 EndX=31 EndY=14.5 EndZ=0
    g17: LineSegment StartX=31 StartY=14.5 StartZ=0 EndX=31 EndY=19.5 EndZ=0
    g18: LineSegment StartX=31 StartY=19.5 StartZ=0 EndX=40 EndY=19.5 EndZ=0
    g19: LineSegment StartX=40 StartY=19.5 StartZ=0 EndX=40 EndY=24.5 EndZ=0
    g20: LineSegment StartX=-66 StartY=14.5 StartZ=0 EndX=-75 EndY=14.5 EndZ=0
    g21: LineSegment StartX=-75 StartY=14.5 StartZ=0 EndX=-75 EndY=19.5 EndZ=0
    g22: LineSegment StartX=-75 StartY=19.5 StartZ=0 EndX=-66 EndY=19.5 EndZ=0
    g23: LineSegment StartX=-66 StartY=19.5 StartZ=0 EndX=-66 EndY=14.5 EndZ=0
  constraints (69):
    c: Coincident(g0,g1)
    c: Coincident(g1,g2)
    c: Coincident(g11,g3)
    c: Coincident(g3,g0)
    c: Horizontal(g0)
    c: Horizontal(g2)
    c: Vertical(g1)
    c: Vertical(g3)
    c: Coincident(g4,g-1)
    c: Diameter(g4) = 17
    c: PointOnObject(g5,g-1)
    c: Diameter(g5) = 8
    c: Distance(g4,g5) = 70
    c: PointOnObject(g6,g-1)
    c: Equal(g6,g7)
    c: Symmetric(g6,g7,g-2)
    c: Diameter(g6) = 4.8
    c: DistanceX(g7,g6) = 59.8
    c: Distance(g0,g-1) = 15
    c: Distance(g11,g-1) = 29.5
    c: Distance(g0,g-2) = 80
    c: Distance(g0,g-2) = 40
    c: Coincident(g8,g9)
    c: Coincident(g9,g10)
    c: Coincident(g2,g10)
    c: Coincident(g11,g8)
    c: Tangent(g2,g11)
    c: Vertical(g8)
    c: Vertical(g10)
    c: Equal(g8,g10)
    c: DistanceX(g9,g9) = 9
    c: DistanceX(g2,g2) = 5
    c: DistanceY(g8,g8) = 5
    c: Distance(g3,g8) = 106
    c: Horizontal(g12)
    c: Coincident(g12,g13)
    c: PointOnObject(g13,g11)
    c: Vertical(g13)
    c: Coincident(g13,g14)
    c: Coincident(g14,g8)
    c: Distance(g13) = 5
    c: Distance(g12) = 9
    c: Coincident(g0,g15)
    c: PointOnObject(g15,g3)
    c: Coincident(g15,g16)
    c: Horizontal(g16)
    c: Coincident(g16,g17)
    c: Vertical(g17)
    c: Coincident(g17,g18)
    c: Horizontal(g18)
    c: Equal(g18,g12)
    c: Equal(g18,g16)
    c: Distance(g17) = 5
    c: Coincident(g19,g18)
    c: Coincident(g19,g12)
    c: Vertical(g19)
    c: Distance(g19) = 5
    c: Coincident(g20,g21)
    c: Coincident(g21,g22)
    c: Coincident(g22,g23)
    c: Coincident(g23,g20)
    c: Horizontal(g20)
    c: Horizontal(g22)
    c: Vertical(g21)
    c: Vertical(g23)
    c: Equal(g9,g22)
    c: Distance(g23) = 5
    c: Distance(g22,g9) = 5
    c: PointOnObject(g21,g10)
FEATURE [PartDesign::Pad] Pad016
  Length = 15
  Length2 = 100
  Placement = pos=(-0.8,0,0) rot=(0.57735,0.57735,-0.57735;4.18879rad)
  Profile = -> Sketch038
  Type = 0
FEATURE [PartDesign::Body] Body014
  Group = -> [Sketch038,Pad016]
  Origin = -> Origin014
  Placement = pos=(170,135,29.5) rot=(0,0,1;0rad)
  Tip = -> Pad016
FEATURE [PartDesign::ShapeBinder] CopyPad016
  Placement = pos=(0,0,0) rot=(0.57735,0.57735,0.57735;2.0944rad)
  TraceSupport = false
FEATURE [Sketcher::SketchObject] Sketch039
  MapMode = 5
  Placement = pos=(-2.64e-14,-60,0) rot=(0.57735,0.57735,-0.57735;2.0944rad)
  Support = -> [CopyPad016]
  sketch-geometry (18):
    g0: LineSegment StartX=29.5 StartY=-16 StartZ=0 EndX=24.5 EndY=-16 EndZ=0
    g1: LineSegment StartX=14.5 StartY=-1 StartZ=0 EndX=4.5 EndY=-1 EndZ=0
    g2: LineSegment StartX=4.5 StartY=-1 StartZ=0 EndX=4.5 EndY=54 EndZ=0
    g3: LineSegment [constr] StartX=4.5 StartY=54 StartZ=0 EndX=29.5 EndY=54 EndZ=0
    g4: LineSegment [constr] StartX=29.5 StartY=54 StartZ=0 EndX=29.5 EndY=-16 EndZ=0
    g5: LineSegment StartX=24.5 StartY=-16 StartZ=0 EndX=24.5 EndY=-1 EndZ=0
    g6: LineSegment StartX=14.5 StartY=-16 StartZ=0 EndX=14.5 EndY=-1 EndZ=0
    g7: LineSegment StartX=24.5 StartY=54 StartZ=0 EndX=24.5 EndY=45 EndZ=0
    g8: LineSegment StartX=24.5 StartY=45 StartZ=0 EndX=29.5 EndY=45 EndZ=0
    g9: LineSegment StartX=29.5 StartY=45 StartZ=0 EndX=29.5 EndY=-16 EndZ=0
    g10: LineSegment StartX=4.5 StartY=54 StartZ=0 EndX=14.5 EndY=54 EndZ=0
    g11: LineSegment StartX=14.5 StartY=54 StartZ=0 EndX=14.5 EndY=45 EndZ=0
    g12: LineSegment StartX=14.5 StartY=45 StartZ=0 EndX=19.5 EndY=45 EndZ=0
    g13: LineSegment StartX=19.5 StartY=45 StartZ=0 EndX=19.5 EndY=54 EndZ=0
    g14: LineSegment StartX=19.5 StartY=54 StartZ=0 EndX=24.5 EndY=54 EndZ=0
    g15: LineSegment StartX=14.5 StartY=-16 StartZ=0 EndX=19.5 EndY=-16 EndZ=0
    g16: LineSegment StartX=19.5 StartY=-16 StartZ=0 EndX=19.5 EndY=-1 EndZ=0
    g17: LineSegment StartX=19.5 StartY=-1 StartZ=0 EndX=24.5 EndY=-1 EndZ=0
  constraints (53):
    c: Horizontal(g0)
    c: Horizontal(g1)
    c: Coincident(g1,g2)
    c: Vertical(g2)
    c: Coincident(g2,g3)
    c: Horizontal(g3)
    c: Coincident(g3,g4)
    c: Coincident(g4,g0)
    c: Vertical(g4)
    c: Distance(g-1,g4) = 29.5
    c: Coincident(g0,g5)
    c: Vertical(g5)
    c: Coincident(g6,g1)
    c: Vertical(g6)
    c: Distance(g5) = 15
    c: Distance(g5,g3) = 55
    c: Distance(g1) = 10
    c: Distance(g6) = 15
    c: Vertical(g7)
    c: Coincident(g7,g8)
    c: PointOnObject(g8,g4)
    c: Horizontal(g8)
    c: Coincident(g8,g9)
    c: Coincident(g9,g0)
    c: Distance(g7) = 9
    c: Distance(g8) = 5
    c: Coincident(g2,g10)
    c: PointOnObject(g10,g3)
    c: Coincident(g10,g11)
    c: Vertical(g11)
    c: Coincident(g11,g12)
    c: Horizontal(g12)
    c: Coincident(g12,g13)
    c: PointOnObject(g13,g3)
    c: Vertical(g13)
    c: Distance(g12) = 5
    c: Coincident(g14,g13)
    c: Coincident(g14,g7)
    c: Horizontal(g14)
    c: Distance(g14) = 5
    c: Equal(g13,g7)
    c: Distance(g0) = 5
    c: Distance(g5,g-1) = 1
    c: Coincident(g6,g15)
    c: Coincident(g15,g16)
    c: Vertical(g16)
    c: Coincident(g16,g17)
    c: Coincident(g17,g5)
    c: Horizontal(g17)
    c: Distance(g17) = 5
    c: Distance(g15) = 5
    c: Horizontal(g15)
    c: Equal(g5,g16)
FEATURE [PartDesign::Pad] Pad017
  Length = 9
  Length2 = 100
  Placement = pos=(0,0,0) rot=(0.57735,0.57735,0.57735;2.0944rad)
  Profile = -> Sketch039
  Type = 0
FEATURE [PartDesign::Body] Body015
  Group = -> [CopyPad016,Sketch039,Pad017]
  Origin = -> Origin015
  Placement = pos=(170,129,29.5) rot=(0,0,1;0rad)
  Tip = -> Pad017
FEATURE [PartDesign::ShapeBinder] CopyPad016001
  Placement = pos=(0,0,0) rot=(0.57735,0.57735,0.57735;2.0944rad)
  TraceSupport = false
FEATURE [Sketcher::SketchObject] Sketch040
  MapMode = 5
  Placement = pos=(1.76e-14,40,0) rot=(0.57735,0.57735,0.57735;4.18879rad)
  Support = -> [CopyPad016001]
  sketch-geometry (15):
    g0: LineSegment [constr] StartX=-29.5 StartY=45 StartZ=0 EndX=-29.5 EndY=-16 EndZ=0
    g1: LineSegment StartX=-29.5 StartY=-16 StartZ=0 EndX=-24.5 EndY=-16 EndZ=0
    g2: LineSegment StartX=-24.5 StartY=-16 StartZ=0 EndX=-24.5 EndY=-1 EndZ=0
    g3: LineSegment StartX=-14.5 StartY=-16 StartZ=0 EndX=-14.5 EndY=45 EndZ=0
    g4: LineSegment [constr] StartX=-14.5 StartY=45 StartZ=0 EndX=-29.5 EndY=45 EndZ=0
    g5: LineSegment StartX=-14.5 StartY=45 StartZ=0 EndX=-19.5 EndY=45 EndZ=0
    g6: LineSegment StartX=-19.5 StartY=45 StartZ=0 EndX=-19.5 EndY=54 EndZ=0
    g7: LineSegment StartX=-29.5 StartY=45 StartZ=0 EndX=-29.5 EndY=-16 EndZ=0
    g8: Circle CenterX=-22.5 CenterY=30 CenterZ=0 NormalX=0 NormalY=0 NormalZ=1 AngleXU=0 Radius=1.5
    g9: LineSegment StartX=-24.5 StartY=-1 StartZ=0 EndX=-19.5 EndY=-1 EndZ=0
    g10: LineSegment StartX=-19.5 StartY=-1 StartZ=0 EndX=-19.5 EndY=-16 EndZ=0
    g11: LineSegment StartX=-19.5 StartY=-16 StartZ=0 EndX=-14.5 EndY=-16 EndZ=0
    g12: LineSegment StartX=-19.5 StartY=54 StartZ=0 EndX=-24.5 EndY=54 EndZ=0
    g13: LineSegment StartX=-24.5 StartY=54 StartZ=0 EndX=-24.5 EndY=45 EndZ=0
    g14: LineSegment StartX=-24.5 StartY=45 StartZ=0 EndX=-29.5 EndY=45 EndZ=0
  constraints (43):
    c: Vertical(g0)
    c: Coincident(g0,g1)
    c: Horizontal(g1)
    c: Coincident(g1,g2)
    c: Vertical(g3)
    c: Coincident(g3,g4)
    c: Coincident(g4,g0)
    c: Horizontal(g4)
    c: Vertical(g2)
    c: Distance(g2) = 15
    c: Distance(g1) = 5
    c: Distance(g0,g-2) = 29.5
    c: Distance(g3,g4) = 61
    c: Coincident(g3,g5)
    c: PointOnObject(g5,g4)
    c: Coincident(g5,g6)
    c: Vertical(g6)
    c: Coincident(g7,g1)
    c: Diameter(g8) = 3
    c: Coincident(g2,g9)
    c: Horizontal(g9)
    c: Coincident(g9,g10)
    c: Vertical(g10)
    c: Coincident(g10,g11)
    c: Horizontal(g11)
    c: Coincident(g3,g11)
    c: Distance(g9) = 5
    c: Distance(g11) = 5
    c: Equal(g2,g10)
    c: Distance(g5) = 5
    c: Coincident(g6,g12)
    c: Coincident(g12,g13)
    c: PointOnObject(g13,g4)
    c: Vertical(g13)
    c: Coincident(g13,g14)
    c: Coincident(g14,g0)
    c: Coincident(g7,g14)
    c: Distance(g12) = 5
    c: Distance(g14) = 5
    c: Distance(g9,g-1) = 1
    c: Distance(g6) = 9
    c: Distance(g8,g4) = 15
    c: Distance(g8,g7) = 7
FEATURE [PartDesign::Pad] Pad018
  Length = 9
  Length2 = 100
  Placement = pos=(0,0,0) rot=(0.57735,0.57735,0.57735;2.0944rad)
  Profile = -> Sketch040
  Reversed = true
  Type = 0
FEATURE [PartDesign::Body] Body016
  Group = -> [CopyPad016001,Sketch040,Pad018]
  Origin = -> Origin016
  Placement = pos=(170,135,29.5) rot=(0,0,1;0rad)
  Tip = -> Pad018
FEATURE [PartDesign::ShapeBinder] CopyPad017
  Placement = pos=(0,0,0) rot=(0.57735,0.57735,0.57735;2.0944rad)
  TraceSupport = false
FEATURE [Sketcher::SketchObject] Sketch041
  MapMode = 5
  Placement = pos=(54,-2.38e-14,1.19e-14) rot=(0.57735,0.57735,0.57735;2.0944rad)
  Support = -> [CopyPad017]
  sketch-geometry (14):
    g0: LineSegment StartX=-75 StartY=-29.5 StartZ=0 EndX=-75 EndY=-24.5 EndZ=0
    g1: LineSegment StartX=-75 StartY=-24.5 StartZ=0 EndX=-66 EndY=-24.5 EndZ=0
    g2: LineSegment StartX=-75 StartY=-14.5 StartZ=0 EndX=40 EndY=-14.5 EndZ=0
    g3: LineSegment StartX=31 StartY=-24.5 StartZ=0 EndX=40 EndY=-24.5 EndZ=0
    g4: LineSegment StartX=40 StartY=-24.5 StartZ=0 EndX=40 EndY=-29.5 EndZ=0
    g5: LineSegment StartX=40 StartY=-29.5 StartZ=0 EndX=-75 EndY=-29.5 EndZ=0
    g6: Circle CenterX=-40 CenterY=-22.5 CenterZ=0 NormalX=0 NormalY=0 NormalZ=1 AngleXU=0 Radius=1.5
    g7: Circle CenterX=-8.1e-15 CenterY=-22.5 CenterZ=0 NormalX=0 NormalY=0 NormalZ=1 AngleXU=0 Radius=1.5
    g8: LineSegment StartX=31 StartY=-24.5 StartZ=0 EndX=31 EndY=-19.5 EndZ=0
    g9: LineSegment StartX=31 StartY=-19.5 StartZ=0 EndX=40 EndY=-19.5 EndZ=0
    g10: LineSegment StartX=40 StartY=-19.5 StartZ=0 EndX=40 EndY=-14.5 EndZ=0
    g11: LineSegment StartX=-66 StartY=-24.5 StartZ=0 EndX=-66 EndY=-19.5 EndZ=0
    g12: LineSegment StartX=-66 StartY=-19.5 StartZ=0 EndX=-75 EndY=-19.5 EndZ=0
    g13: LineSegment StartX=-75 StartY=-19.5 StartZ=0 EndX=-75 EndY=-14.5 EndZ=0
  constraints (42):
    c: Vertical(g0)
    c: Coincident(g0,g1)
    c: Horizontal(g1)
    c: Horizontal(g2)
    c: Horizontal(g3)
    c: Coincident(g3,g4)
    c: Vertical(g4)
    c: Coincident(g4,g5)
    c: Coincident(g5,g0)
    c: Horizontal(g5)
    c: Distance(g1) = 9
    c: Distance(g0) = 5
    c: Distance(g4) = 5
    c: Distance(g3) = 9
    c: Distance(g-1,g5) = 29.5
    c: Distance(g4,g-2) = 40
    c: Equal(g6,g7)
    c: Distance(g6,g7) = 40
    c: Diameter(g6) = 3
    c: Coincident(g3,g8)
    c: Coincident(g8,g9)
    c: Horizontal(g9)
    c: Coincident(g9,g10)
    c: Vertical(g10)
    c: Coincident(g2,g10)
    c: Distance(g8) = 5
    c: Distance(g10) = 5
    c: Equal(g3,g9)
    c: Vertical(g8)
    c: Coincident(g1,g11)
    c: Coincident(g11,g12)
    c: Coincident(g12,g13)
    c: Coincident(g13,g2)
    c: Vertical(g13)
    c: Horizontal(g12)
    c: Distance(g13) = 5
    c: Distance(g11) = 5
    c: Equal(g1,g12)
    c: Distance(g5) = 115
    c: Distance(g7,g5) = 7
    c: Distance(g6,g5) = 7
    c: Distance(g7,g4) = 40
FEATURE [PartDesign::Pad] Pad019
  Length = 9
  Length2 = 100
  Placement = pos=(0,0,0) rot=(0.57735,0.57735,0.57735;2.0944rad)
  Profile = -> Sketch041
  Reversed = true
  Type = 0
FEATURE [PartDesign::Body] Body017
  Group = -> [CopyPad017,Sketch041,Pad019]
  Origin = -> Origin017
  Placement = pos=(170,135,29.5) rot=(0,0,1;0rad)
  Tip = -> Pad019
FEATURE [PartDesign::CoordinateSystem] LCS_1
  AttacherType = Attacher::AttachEngine3D
  MapMode = 2
  Support = -> [X_Axis019]
FEATURE [Sketcher::SketchObject] Sketch042
  MapMode = 5
  Placement = pos=(0,0,0) rot=(0.57735,0.57735,0.57735;2.0944rad)
  Support = -> [YZ_Plane018]
  sketch-geometry (28):
    g0: LineSegment [constr] StartX=20 StartY=20 StartZ=0 EndX=-20 EndY=20 EndZ=0
    g1: LineSegment [constr] StartX=-20 StartY=20 StartZ=0 EndX=-20 EndY=-20 EndZ=0
    g2: LineSegment [constr] StartX=-20 StartY=-20 StartZ=0 EndX=20 EndY=-20 EndZ=0
    g3: LineSegment [constr] StartX=20 StartY=-20 StartZ=0 EndX=20 EndY=20 EndZ=0
    g4: LineSegment [constr] StartX=3.69504 StartY=-6.4 StartZ=0 EndX=7.39008 EndY=0 EndZ=0
    g5: LineSegment [constr] StartX=7.39008 StartY=0 StartZ=0 EndX=3.69504 EndY=6.4 EndZ=0
    g6: LineSegment [constr] StartX=3.69504 StartY=6.4 StartZ=0 EndX=-3.69504 EndY=6.4 EndZ=0
    g7: LineSegment [constr] StartX=-3.69504 StartY=6.4 StartZ=0 EndX=-7.39008 EndY=-7.416e-13 EndZ=0
    g8: LineSegment [constr] StartX=-7.39008 StartY=-7.416e-13 StartZ=0 EndX=-3.69504 EndY=-6.4 EndZ=0
    g9: LineSegment [constr] StartX=-3.69504 StartY=-6.4 StartZ=0 EndX=3.69504 EndY=-6.4 EndZ=0
    g10: Circle [constr] CenterX=0 CenterY=0 CenterZ=0 NormalX=0 NormalY=0 NormalZ=1 AngleXU=0 Radius=7.39008
    g11: LineSegment StartX=-20 StartY=20 StartZ=0 EndX=-7.5 EndY=20 EndZ=0
    g12: LineSegment StartX=-7.5 StartY=20 StartZ=0 EndX=-7.5 EndY=35 EndZ=0
    g13: LineSegment StartX=-7.5 StartY=35 StartZ=0 EndX=7.5 EndY=35 EndZ=0
    g14: LineSegment StartX=7.5 StartY=35 StartZ=0 EndX=7.5 EndY=20 EndZ=0
    g15: LineSegment StartX=7.5 StartY=20 StartZ=0 EndX=20 EndY=20 EndZ=0
    g16: Circle CenterX=0 CenterY=0 CenterZ=0 NormalX=0 NormalY=0 NormalZ=1 AngleXU=0 Radius=4.15
    g17: LineSegment StartX=-20 StartY=20 StartZ=0 EndX=-20 EndY=-5 EndZ=0
    g18: LineSegment StartX=-20 StartY=-5 StartZ=0 EndX=-15 EndY=-5 EndZ=0
    g19: LineSegment StartX=-20 StartY=-20 StartZ=0 EndX=20 EndY=-20 EndZ=0
    g20: LineSegment StartX=15 StartY=-5 StartZ=0 EndX=20 EndY=-5 EndZ=0
    g21: LineSegment StartX=20 StartY=-5 StartZ=0 EndX=20 EndY=20 EndZ=0
    g22: LineSegment StartX=-15 StartY=-5 StartZ=0 EndX=-15 EndY=-14 EndZ=0
    g23: LineSegment StartX=-15 StartY=-14 StartZ=0 EndX=-20 EndY=-14 EndZ=0
    g24: LineSegment StartX=-20 StartY=-14 StartZ=0 EndX=-20 EndY=-20 EndZ=0
    g25: LineSegment StartX=20 StartY=-20 StartZ=0 EndX=20 EndY=-14 EndZ=0
    g26: LineSegment StartX=20 StartY=-14 StartZ=0 EndX=15 EndY=-14 EndZ=0
    g27: LineSegment StartX=15 StartY=-14 StartZ=0 EndX=15 EndY=-5 EndZ=0
  constraints (72):
    c: Coincident(g0,g1)
    c: Coincident(g1,g2)
    c: Coincident(g2,g3)
    c: Coincident(g3,g0)
    c: Horizontal(g2)
    c: Vertical(g1)
    c: Vertical(g3)
    c: Coincident(g4,g5)
    c: Coincident(g5,g6)
    c: Coincident(g6,g7)
    c: Coincident(g7,g8)
    c: Coincident(g8,g9)
    c: Coincident(g9,g4)
    c: Equal(g4, g5-g9) x5
    c: PointOnObject(g4,g10)
    c: PointOnObject(g5,g10)
    c: PointOnObject(g6,g10)
    c: PointOnObject(g7,g10)
    c: PointOnObject(g8,g10)
    c: PointOnObject(g9,g10)
    c: Coincident(g10,g-1)
    c: Distance(g-1,g5) = 6.4
    c: PointOnObject(g4,g-1)
    c: Coincident(g1,g11)
    c: PointOnObject(g11,g0)
    c: Coincident(g11,g12)
    c: Coincident(g12,g13)
    c: Coincident(g13,g14)
    c: Coincident(g14,g15)
    c: Coincident(g15,g3)
    c: Horizontal(g13)
    c: Vertical(g12)
    c: Vertical(g14)
    c: Distance(g12) = 15
    c: Distance(g13) = 15
    c: Symmetric(g1,g3,g-2)
    c: Symmetric(g11,g14,g-2)
    c: Distance(g3,g-1) = 20
    c: Distance(g2,g-1) = 20
    c: DistanceX(g2,g2) = 40
    c: Coincident(g16,g-1)
    c: Diameter(g16) = 8.3
    c: Coincident(g11,g17)
    c: PointOnObject(g17,g1)
    c: Coincident(g17,g18)
    c: PointOnObject(g20,g3)
    c: Horizontal(g20)
    c: Coincident(g20,g21)
    c: Coincident(g21,g15)
    c: Horizontal(g18)
    c: Distance(g18) = 5
    c: Distance(g20) = 5
    c: Coincident(g18,g22)
    c: Vertical(g22)
    c: Coincident(g22,g23)
    c: PointOnObject(g23,g1)
    c: Coincident(g23,g24)
    c: Coincident(g24,g1)
    c: Coincident(g2,g25)
    c: Vertical(g25)
    c: Coincident(g25,g26)
    c: Coincident(g26,g27)
    c: Coincident(g27,g20)
    c: Vertical(g27)
    c: Horizontal(g23)
    c: Horizontal(g26)
    c: Coincident(g19,g25)
    c: Coincident(g19,g24)
    c: Distance(g27) = 9
    c: Distance(g25) = 6
    c: Equal(g27,g22)
    c: Equal(g25,g24)
FEATURE [PartDesign::Pad] Pad020
  Length = 15
  Length2 = 100
  Placement = pos=(0,0,0) rot=(0.57735,0.57735,0.57735;2.0944rad)
  Profile = -> Sketch042
  Type = 0
FEATURE [PartDesign::ShapeBinder] CopyPocket014
  Placement = pos=(0,0,0) rot=(0.57735,0.57735,0.57735;2.0944rad)
  TraceSupport = false
FEATURE [Sketcher::SketchObject] Sketch044
  MapMode = 5
  Placement = pos=(1.69e-14,1.33e-14,-5) rot=(0.707107,0.707107,0;3.14159rad)
  Support = -> [CopyPocket014]
  sketch-geometry (8):
    g0: LineSegment StartX=-20 StartY=-29 StartZ=0 EndX=-20 EndY=15 EndZ=0
    g1: LineSegment StartX=-20 StartY=15 StartZ=0 EndX=-15 EndY=15 EndZ=0
    g2: LineSegment StartX=-15 StartY=15 StartZ=0 EndX=-15 EndY=0 EndZ=0
    g3: LineSegment StartX=-15 StartY=0 StartZ=0 EndX=-10 EndY=0 EndZ=0
    g4: LineSegment StartX=-10 StartY=0 StartZ=0 EndX=-10 EndY=-14 EndZ=0
    g5: LineSegment StartX=-10 StartY=-14 StartZ=0 EndX=-15 EndY=-14 EndZ=0
    g6: LineSegment StartX=-15 StartY=-14 StartZ=0 EndX=-15 EndY=-29 EndZ=0
    g7: LineSegment StartX=-15 StartY=-29 StartZ=0 EndX=-20 EndY=-29 EndZ=0
  constraints (24):
    c: Vertical(g0)
    c: Coincident(g0,g1)
    c: Horizontal(g1)
    c: Coincident(g1,g2)
    c: PointOnObject(g2,g-1)
    c: Vertical(g2)
    c: Coincident(g2,g3)
    c: PointOnObject(g3,g-1)
    c: Coincident(g3,g4)
    c: Vertical(g4)
    c: Coincident(g4,g5)
    c: Horizontal(g5)
    c: Coincident(g5,g6)
    c: Vertical(g6)
    c: Coincident(g6,g7)
    c: Coincident(g7,g0)
    c: Horizontal(g7)
    c: Distance(g1) = 5
    c: Distance(g7) = 5
    c: Distance(g6) = 15
    c: Distance(g2) = 15
    c: Distance(g4) = 14
    c: Distance(g0,g-2) = 20
    c: Distance(g3) = 5
FEATURE [PartDesign::Pad] Pad021
  Length = 9
  Length2 = 100
  Placement = pos=(0,0,0) rot=(0.57735,0.57735,0.57735;2.0944rad)
  Profile = -> Sketch044
  Type = 0
FEATURE [PartDesign::Body] Body020
  Group = -> [CopyPocket014,Sketch044,Pad021]
  Origin = -> Origin021
  Placement = pos=(100,135,29.5) rot=(0,0,1;0rad)
  Tip = -> Pad021
FEATURE [PartDesign::CoordinateSystem] LCS_1001
  AttacherType = Attacher::AttachEngine3D
  MapMode = 2
  Support = -> [X_Axis023]
FEATURE [PartDesign::ShapeBinder] CopyPocket014001
  Placement = pos=(0,0,0) rot=(0.57735,0.57735,0.57735;2.0944rad)
  TraceSupport = false
FEATURE [Sketcher::SketchObject] Sketch045
  MapMode = 5
  Placement = pos=(-1.186e-13,-9.34e-14,35) rot=(0,0,-1;1.5708rad)
  Support = -> [CopyPocket014001]
  sketch-geometry (47):
    g0: LineSegment [constr] StartX=-64 StartY=80 StartZ=0 EndX=91 EndY=80 EndZ=0
    g1: LineSegment [constr] StartX=91 StartY=80 StartZ=0 EndX=91 EndY=-95 EndZ=0
    g2: LineSegment StartX=91 StartY=-95 StartZ=0 EndX=-64 EndY=-95 EndZ=0
    g3: LineSegment StartX=-64 StartY=-95 StartZ=0 EndX=-64 EndY=80 EndZ=0
    g4: LineSegment StartX=-7.5 StartY=15 StartZ=0 EndX=7.5 EndY=15 EndZ=0
    g5: LineSegment StartX=7.5 StartY=15 StartZ=0 EndX=7.5 EndY=0 EndZ=0
    g6: LineSegment StartX=7.5 StartY=0 StartZ=0 EndX=-7.5 EndY=0 EndZ=0
    g7: LineSegment StartX=-7.5 StartY=0 StartZ=0 EndX=-7.5 EndY=15 EndZ=0
    g8: LineSegment StartX=-7.5 StartY=-14 StartZ=0 EndX=7.5 EndY=-14 EndZ=0
    g9: LineSegment StartX=7.5 StartY=-14 StartZ=0 EndX=7.5 EndY=-29 EndZ=0
    g10: LineSegment StartX=7.5 StartY=-29 StartZ=0 EndX=-7.5 EndY=-29 EndZ=0
    g11: LineSegment StartX=-7.5 StartY=-29 StartZ=0 EndX=-7.5 EndY=-14 EndZ=0
    g12: Circle CenterX=35 CenterY=-52 CenterZ=0 NormalX=0 NormalY=0 NormalZ=1 AngleXU=0 Radius=9.5
    g13: LineSegment StartX=91 StartY=-95 StartZ=0 EndX=91 EndY=-60 EndZ=0
    g14: LineSegment StartX=91 StartY=-60 StartZ=0 EndX=82 EndY=-60 EndZ=0
    g15: LineSegment StartX=82 StartY=-60 StartZ=0 EndX=82 EndY=-40 EndZ=0
    g16: LineSegment StartX=82 StartY=-40 StartZ=0 EndX=91 EndY=-40 EndZ=0
    g17: LineSegment StartX=91 StartY=-40 StartZ=0 EndX=91 EndY=61 EndZ=0
    g18: LineSegment StartX=91 StartY=61 StartZ=0 EndX=82 EndY=61 EndZ=0
    g19: LineSegment StartX=42 StartY=71 StartZ=0 EndX=42 EndY=80 EndZ=0
    g20: LineSegment StartX=42 StartY=80 StartZ=0 EndX=32 EndY=80 EndZ=0
    g21: LineSegment StartX=32 StartY=80 StartZ=0 EndX=32 EndY=71 EndZ=0
    g22: LineSegment StartX=32 StartY=71 StartZ=0 EndX=12 EndY=71 EndZ=0
    g23: LineSegment StartX=12 StartY=71 StartZ=0 EndX=12 EndY=80 EndZ=0
    g24: LineSegment StartX=12 StartY=80 StartZ=0 EndX=2 EndY=80 EndZ=0
    g25: LineSegment StartX=2 StartY=80 StartZ=0 EndX=2 EndY=71 EndZ=0
    g26: LineSegment StartX=2 StartY=71 StartZ=0 EndX=-18 EndY=71 EndZ=0
    g27: LineSegment StartX=-18 StartY=71 StartZ=0 EndX=-18 EndY=80 EndZ=0
    g28: LineSegment StartX=-18 StartY=80 StartZ=0 EndX=-28 EndY=80 EndZ=0
    g29: LineSegment StartX=-28 StartY=71 StartZ=0 EndX=-48 EndY=71 EndZ=0
    g30: LineSegment StartX=-48 StartY=71 StartZ=0 EndX=-48 EndY=80 EndZ=0
    g31: LineSegment StartX=-48 StartY=80 StartZ=0 EndX=-64 EndY=80 EndZ=0
    g32: LineSegment StartX=-28 StartY=71 StartZ=0 EndX=-28 EndY=80 EndZ=0
    g33: LineSegment StartX=65 StartY=-73 StartZ=0 EndX=75 EndY=-73 EndZ=0
    g34: LineSegment StartX=75 StartY=-73 StartZ=0 EndX=75 EndY=-88 EndZ=0
    g35: LineSegment StartX=75 StartY=-88 StartZ=0 EndX=65 EndY=-88 EndZ=0
    g36: LineSegment StartX=65 StartY=-88 StartZ=0 EndX=65 EndY=-73 EndZ=0
    g37: LineSegment StartX=65 StartY=40 StartZ=0 EndX=75 EndY=40 EndZ=0
    g38: LineSegment StartX=75 StartY=40 StartZ=0 EndX=75 EndY=25 EndZ=0
    g39: LineSegment StartX=75 StartY=25 StartZ=0 EndX=65 EndY=25 EndZ=0
    g40: LineSegment StartX=65 StartY=25 StartZ=0 EndX=65 EndY=40 EndZ=0
    g41: LineSegment StartX=82 StartY=61 StartZ=0 EndX=82 EndY=71 EndZ=0
    g42: LineSegment StartX=82 StartY=71 StartZ=0 EndX=91 EndY=71 EndZ=0
    g43: LineSegment StartX=91 StartY=71 StartZ=0 EndX=91 EndY=80 EndZ=0
    g44: LineSegment StartX=91 StartY=80 StartZ=0 EndX=62 EndY=80 EndZ=0
    g45: LineSegment StartX=62 StartY=80 StartZ=0 EndX=62 EndY=71 EndZ=0
    g46: LineSegment StartX=62 StartY=71 StartZ=0 EndX=42 EndY=71 EndZ=0
  constraints (139):
    c: Coincident(g0,g1)
    c: Coincident(g1,g2)
    c: Coincident(g2,g3)
    c: Coincident(g3,g0)
    c: Horizontal(g0)
    c: Horizontal(g2)
    c: Vertical(g1)
    c: Vertical(g3)
    c: Coincident(g4,g5)
    c: Coincident(g5,g6)
    c: Coincident(g6,g7)
    c: Coincident(g7,g4)
    c: Horizontal(g4)
    c: Horizontal(g6)
    c: Vertical(g5)
    c: Vertical(g7)
    c: Coincident(g8,g9)
    c: Coincident(g9,g10)
    c: Coincident(g10,g11)
    c: Coincident(g11,g8)
    c: Horizontal(g10)
    c: Vertical(g9)
    c: Vertical(g11)
    c: Distance(g5) = 15
    c: Distance(g4) = 15
    c: Distance(g8) = 15
    c: Distance(g9) = 15
    c: Distance(g8,g6) = 14
    c: Symmetric(g6,g5,g-1)
    c: Symmetric(g8,g8,g-2)
    c: Diameter(g12) = 19
    c: Distance(g12,g-1) = 52
    c: Distance(g12,g-2) = 35
    c: Coincident(g2,g13)
    c: PointOnObject(g13,g1)
    c: Coincident(g13,g14)
    c: Horizontal(g14)
    c: Coincident(g14,g15)
    c: Coincident(g15,g16)
    c: PointOnObject(g16,g1)
    c: Horizontal(g16)
    c: Vertical(g15)
    c: Vertical(g17)
    c: Coincident(g17,g18)
    c: DistanceY(g15,g15) = 20
    c: Horizontal(g18)
    c: DistanceX(g14,g14) = 9
    c: DistanceY(g-1,g2) = -95
    c: DistanceY(g17,g0) = 19
    c: DistanceY(g3,g3) = 175
    c: Coincident(g19,g20)
    c: Coincident(g21,g22)
    c: Coincident(g22,g23)
    c: Coincident(g23,g24)
    c: Coincident(g25,g26)
    c: Coincident(g27,g28)
    c: Coincident(g29,g30)
    c: Vertical(g30)
    c: Coincident(g30,g31)
    c: Coincident(g31,g3)
    c: Coincident(g32,g29)
    c: Coincident(g32,g28)
    c: Horizontal(g28)
    c: Horizontal(g29)
    c: Horizontal(g26)
    c: Vertical(g21)
    c: Vertical(g23)
    c: Vertical(g32)
    c: Coincident(g26,g27)
    c: Coincident(g21,g20)
    c: Vertical(g25)
    c: Vertical(g19)
    c: Horizontal(g22)
    c: Horizontal(g20)
    c: Horizontal(g24)
    c: Coincident(g25,g24)
    c: PointOnObject(g19,g0)
    c: PointOnObject(g23,g0)
    c: PointOnObject(g27,g0)
    c: Equal(g32,g27)
    c: Equal(g25,g23)
    c: Equal(g19,g21)
    c: Equal(g29,g26)
    c: Equal(g26,g22)
    c: Vertical(g27)
    c: Equal(g20,g24)
    c: Equal(g24,g28)
    c: Distance(g29,g0) = 9
    c: DistanceX(g20,g20) = 10
    c: Equal(g24,g20)
    c: Equal(g28,g24)
    c: DistanceX(g22,g22) = 20
    c: Horizontal(g31)
    c: Coincident(g33,g34)
    c: Coincident(g34,g35)
    c: Coincident(g35,g36)
    c: Coincident(g36,g33)
    c: Horizontal(g33)
    c: Horizontal(g35)
    c: Vertical(g34)
    c: Vertical(g36)
    c: DistanceY(g34,g34) = 15
    c: DistanceX(g35,g35) = 10
    c: Distance(g34,g2) = 7
    c: Distance(g34,g13) = 16
    c: Coincident(g37,g38)
    c: Coincident(g38,g39)
    c: Coincident(g39,g40)
    c: Coincident(g40,g37)
    c: Horizontal(g37)
    c: Horizontal(g39)
    c: Vertical(g38)
    c: Vertical(g40)
    c: DistanceY(g38,g38) = 15
    c: DistanceX(g37,g37) = 10
    c: Distance(g37,g17) = 16
    c: Coincident(g17,g16)
    c: Coincident(g41,g18)
    c: Vertical(g41)
    c: DistanceX(g18,g18) = 9
    c: DistanceY(g17,g17) = 101
    c: DistanceX(g-2,g2) = 91
    c: DistanceX(g2,g2) = 155
    c: DistanceX(g19,g41) = 40
    c: Distance(g37,g0) = 40
    c: Coincident(g41,g42)
    c: PointOnObject(g42,g1)
    c: Horizontal(g42)
    c: Coincident(g42,g43)
    c: Coincident(g43,g0)
    c: Coincident(g43,g44)
    c: PointOnObject(g44,g0)
    c: Coincident(g44,g45)
    c: Vertical(g45)
    c: Coincident(g45,g46)
    c: Coincident(g46,g19)
    c: Horizontal(g46)
    c: DistanceX(g44,g44) = 29
    c: DistanceY(g41,g41) = 10
FEATURE [PartDesign::Pad] Pad022
  Length = 15
  Length2 = 100
  Placement = pos=(0,0,0) rot=(0.57735,0.57735,0.57735;2.0944rad)
  Profile = -> Sketch045
  Reversed = true
  Type = 0
FEATURE [Sketcher::SketchObject] Sketch046
  MapMode = 5
  Placement = pos=(0,0,0) rot=(0.57735,0.57735,0.57735;2.0944rad)
  Support = -> [YZ_Plane025]
  sketch-geometry (16):
    g0: LineSegment StartX=-85 StartY=20 StartZ=0 EndX=-75 EndY=20 EndZ=0
    g1: LineSegment StartX=-75 StartY=20 StartZ=0 EndX=-75 EndY=35 EndZ=0
    g2: LineSegment StartX=-75 StartY=35 StartZ=0 EndX=-65 EndY=35 EndZ=0
    g3: LineSegment StartX=-65 StartY=35 StartZ=0 EndX=-65 EndY=20 EndZ=0
    g4: LineSegment StartX=-65 StartY=20 StartZ=0 EndX=-55 EndY=20 EndZ=0
    g5: LineSegment StartX=-55 StartY=20 StartZ=0 EndX=-55 EndY=-15 EndZ=0
    g6: LineSegment StartX=-55 StartY=-15 StartZ=0 EndX=-85 EndY=-15 EndZ=0
    g7: LineSegment StartX=-85 StartY=-15 StartZ=0 EndX=-85 EndY=20 EndZ=0
    g8: LineSegment [constr] StartX=-70 StartY=35 StartZ=0 EndX=-70 EndY=-15 EndZ=0
    g9: LineSegment StartX=-62.6099 StartY=0 StartZ=0 EndX=-66.305 EndY=6.4 EndZ=0
    g10: LineSegment StartX=-66.305 StartY=6.4 StartZ=0 EndX=-73.695 EndY=6.4 EndZ=0
    g11: LineSegment StartX=-73.695 StartY=6.4 StartZ=0 EndX=-77.3901 EndY=2.487e-13 EndZ=0
    g12: LineSegment StartX=-77.3901 StartY=2.487e-13 StartZ=0 EndX=-73.695 EndY=-6.4 EndZ=0
    g13: LineSegment StartX=-73.695 StartY=-6.4 StartZ=0 EndX=-66.305 EndY=-6.4 EndZ=0
    g14: LineSegment StartX=-66.305 StartY=-6.4 StartZ=0 EndX=-62.6099 EndY=0 EndZ=0
    g15: Circle [constr] CenterX=-70 CenterY=0 CenterZ=0 NormalX=0 NormalY=0 NormalZ=1 AngleXU=0 Radius=7.39008
  constraints (45):
    c: Horizontal(g0)
    c: Coincident(g0,g1)
    c: Vertical(g1)
    c: Coincident(g1,g2)
    c: Horizontal(g2)
    c: Coincident(g2,g3)
    c: Vertical(g3)
    c: Coincident(g3,g4)
    c: Horizontal(g4)
    c: Coincident(g4,g5)
    c: Vertical(g5)
    c: Coincident(g5,g6)
    c: Horizontal(g6)
    c: Coincident(g6,g7)
    c: Coincident(g7,g0)
    c: Vertical(g7)
    c: Distance(g1) = 15
    c: Distance(g2) = 10
    c: Distance(g0) = 10
    c: Distance(g4) = 10
    c: PointOnObject(g8,g2)
    c: PointOnObject(g8,g6)
    c: Symmetric(g1,g2,g8)
    c: Equal(g3,g1)
    c: Distance(g4,g-1) = 20
    c: Distance(g-1,g8) = 70
    c: Distance(g7) = 35
    c: Coincident(g9,g10)
    c: Coincident(g10,g11)
    c: Coincident(g11,g12)
    c: Coincident(g12,g13)
    c: Coincident(g13,g14)
    c: Coincident(g14,g9)
    c: Equal(g9, g10-g14) x5
    c: PointOnObject(g9,g15)
    c: PointOnObject(g10,g15)
    c: PointOnObject(g11,g15)
    c: PointOnObject(g12,g15)
    c: PointOnObject(g13,g15)
    c: PointOnObject(g14,g15)
    c: PointOnObject(g15,g-1)
    c: PointOnObject(g15,g8)
    c: Distance(g15,g10) = 6.4
    c: PointOnObject(g9,g-1)
    c: Distance(g13,g6) = 8.6
FEATURE [PartDesign::Pad] Pad023
  Length = 15
  Length2 = 100
  Placement = pos=(0,0,0) rot=(0.57735,0.57735,0.57735;2.0944rad)
  Profile = -> Sketch046
  Type = 0
FEATURE [PartDesign::Body] Body023
  Group = -> [Sketch046,Pad023]
  Origin = -> Origin025
  Placement = pos=(125,135,29.5) rot=(0,0,1;0rad)
  Tip = -> Pad023
FEATURE [PartDesign::FeatureBase] Clone002
  BaseFeature = -> Body023
  Placement = pos=(12,135,29.5) rot=(0,0,1;0rad)
FEATURE [PartDesign::Body] Body024
  BaseFeature = -> Body023
  Group = -> [Clone002]
  Origin = -> Origin026
  Tip = -> Clone002
FEATURE [PartDesign::CoordinateSystem] LCS_1002
  AttacherType = Attacher::AttachEngine3D
  MapMode = 2
  Support = -> [X_Axis027]
FEATURE [App::Part] dosierer
  Group = -> [LCS_1002,Body002,Body003,Body001]
  Origin = -> Origin027
  Placement = pos=(97,139,211) rot=(0,0,1;3.14159rad)
FEATURE [Sketcher::SketchObject] Sketch047
  MapMode = 5
  Support = -> [XY_Plane028]
  sketch-geometry (1):
    g0: Circle CenterX=0 CenterY=0 CenterZ=0 NormalX=0 NormalY=0 NormalZ=1 AngleXU=0 Radius=4
  constraints (2):
    c: Coincident(g0,g-1)
    c: Diameter(g0) = 8
FEATURE [PartDesign::Pad] Pad024
  Length = 168
  Length2 = 100
  Profile = -> Sketch047
  Type = 0
FEATURE [PartDesign::Body] Body025  label="gewindestange-vertikal"
  Group = -> [Sketch047,Pad024]
  Origin = -> Origin028
  Placement = pos=(48,100,86) rot=(0,0,1;0rad)
  Tip = -> Pad024
FEATURE [TechDraw::DrawSVGTemplate] Template
  EditableTexts = Designed_by_Name=Designed by Name; Drawing_number=Drawing number; FC-Date=Date; FC-SC=Scale; FC-SH=Sheet; FC-Title=Title; Subtitle=Subtitle; Weight=Weight
  Height = 210
  Orientation = 1
  Width = 297
FEATURE [TechDraw::DrawProjGroupItem] ProjItem  label="Front"
  CoarseView = false
  Direction = (-1,0,0)
  Focus = 100
  HardHidden = false
  IsoCount = 0
  IsoHidden = false
  IsoVisible = false
  LockPosition = true
  Perspective = false
  Rotation = 0
  RotationVector = (0,-1,0)
  ScaleType = 2
  SeamHidden = false
  SeamVisible = false
  SmoothHidden = false
  SmoothVisible = false
  Source = -> [Body014]
  Type = 0
  X = 0
  XDirection = (0,-1,0)
  Y = 0
FEATURE [TechDraw::DrawProjGroupItem] ProjItem001  label="Top"
  CoarseView = false
  Direction = (0,0,1)
  Focus = 100
  HardHidden = false
  IsoCount = 0
  IsoHidden = false
  IsoVisible = false
  LockPosition = false
  Perspective = false
  Rotation = 0
  RotationVector = (1,0,0)
  ScaleType = 2
  SeamHidden = false
  SeamVisible = false
  SmoothHidden = false
  SmoothVisible = false
  Source = -> [Body014]
  Type = 4
  X = 0
  XDirection = (0,-1,0)
  Y = -59.5
FEATURE [TechDraw::DrawProjGroupItem] ProjItem002  label="Left"
  CoarseView = false
  Direction = (-1e-16,1,0)
  Focus = 100
  HardHidden = false
  IsoCount = 0
  IsoHidden = false
  IsoVisible = false
  LockPosition = false
  Perspective = false
  Rotation = 0
  RotationVector = (1,0,0)
  ScaleType = 2
  SeamHidden = false
  SeamVisible = false
  SmoothHidden = false
  SmoothVisible = false
  Source = -> [Body014]
  Type = 1
  X = 135
  XDirection = (-1,-1e-16,0)
  Y = 0
FEATURE [TechDraw::DrawProjGroup] ProjGroup
  Anchor = -> ProjItem
  AutoDistribute = true
  LockPosition = false
  ProjectionType = 0
  Rotation = 0
  ScaleType = 0
  Source = -> [Body014]
  Views = -> [ProjItem,ProjItem001,ProjItem002]
  X = 101.474
  Y = 148.82
  spacingX = 15
  spacingY = 15
FEATURE [TechDraw::DrawViewDimension] Dimension
  Arbitrary = false
  FormatSpec = %.3f
  Inverted = false
  LockPosition = false
  MeasureType = 1
  OverTolerance = 0
  References2D = -> [ProjItem]
  Rotation = 0
  ScaleType = 0
  TheoreticalExact = false
  Type = 1
  UnderTolerance = 0
  X = 15
  Y = 31.1157
FEATURE [TechDraw::DrawViewDimension] Dimension001
  Arbitrary = false
  FormatSpec = %.3f
  Inverted = false
  LockPosition = false
  MeasureType = 1
  OverTolerance = 0
  References2D = -> [ProjItem]
  Rotation = 0
  ScaleType = 0
  TheoreticalExact = false
  Type = 2
  UnderTolerance = 0
  X = -67.3555
  Y = 18.1325
FEATURE [TechDraw::DrawViewDimension] Dimension002
  Arbitrary = false
  FormatSpec = %.3f
  Inverted = false
  LockPosition = false
  MeasureType = 1
  OverTolerance = 0
  References2D = -> [ProjItem]
  Rotation = 0
  ScaleType = 0
  TheoreticalExact = false
  Type = 1
  UnderTolerance = 0
  X = -37.745
  Y = 31.1157
FEATURE [TechDraw::DrawViewDimension] Dimension003
  Arbitrary = false
  FormatSpec = %.3f
  Inverted = false
  LockPosition = false
  MeasureType = 1
  OverTolerance = 0
  References2D = -> [ProjItem]
  Rotation = 0
  ScaleType = 0
  TheoreticalExact = false
  Type = 1
  UnderTolerance = 0
  X = 62.1409
  Y = 31.3036
FEATURE [TechDraw::DrawViewDimension] Dimension004
  Arbitrary = false
  FormatSpec = %.3f
  Inverted = false
  LockPosition = false
  MeasureType = 1
  OverTolerance = 0
  References2D = -> [ProjItem]
  Rotation = 0
  ScaleType = 0
  TheoreticalExact = false
  Type = 2
  UnderTolerance = 0
  X = -67.1676
  Y = -7.87584
FEATURE [Sketcher::SketchObject] Sketch048
  MapMode = 5
  Placement = pos=(0,0,0) rot=(0.57735,0.57735,0.57735;2.0944rad)
  Support = -> [YZ_Plane029]
  sketch-geometry (22):
    g0: LineSegment StartX=-40 StartY=15 StartZ=0 EndX=80 EndY=15 EndZ=0
    g1: LineSegment StartX=80 StartY=15 StartZ=0 EndX=80 EndY=-29.5 EndZ=0
    g2: LineSegment [constr] StartX=80 StartY=-29.5 StartZ=0 EndX=-40 EndY=-29.5 EndZ=0
    g3: LineSegment [constr] StartX=-40 StartY=-29.5 StartZ=0 EndX=-40 EndY=15 EndZ=0
    g4: Circle CenterX=70 CenterY=0 CenterZ=0 NormalX=0 NormalY=0 NormalZ=1 AngleXU=0 Radius=4.05
    g5: LineSegment StartX=7.39008 StartY=0 StartZ=0 EndX=3.69504 EndY=6.4 EndZ=0
    g6: LineSegment StartX=3.69504 StartY=6.4 StartZ=0 EndX=-3.69504 EndY=6.4 EndZ=0
    g7: LineSegment StartX=-3.69504 StartY=6.4 StartZ=0 EndX=-7.39008 EndY=-9e-16 EndZ=0
    g8: LineSegment StartX=-7.39008 StartY=-9e-16 StartZ=0 EndX=-3.69504 EndY=-6.4 EndZ=0
    g9: LineSegment StartX=-3.69504 StartY=-6.4 StartZ=0 EndX=3.69504 EndY=-6.4 EndZ=0
    g10: LineSegment StartX=3.69504 StartY=-6.4 StartZ=0 EndX=7.39008 EndY=0 EndZ=0
    g11: Circle [constr] CenterX=0 CenterY=0 CenterZ=0 NormalX=0 NormalY=0 NormalZ=1 AngleXU=0 Radius=7.39008
    g12: LineSegment StartX=-40 StartY=15 StartZ=0 EndX=-40 EndY=-14.5 EndZ=0
    g13: LineSegment StartX=-31 StartY=-29.5 StartZ=0 EndX=80 EndY=-29.5 EndZ=0
    g14: Circle CenterX=10 CenterY=-14.5 CenterZ=0 NormalX=0 NormalY=0 NormalZ=1 AngleXU=0 Radius=1.5
    g15: Circle CenterX=60 CenterY=-14.5 CenterZ=0 NormalX=0 NormalY=0 NormalZ=1 AngleXU=0 Radius=1.5
    g16: LineSegment StartX=-31 StartY=-29.5 StartZ=0 EndX=-31 EndY=-24.5 EndZ=0
    g17: LineSegment StartX=-31 StartY=-24.5 StartZ=0 EndX=-40 EndY=-24.5 EndZ=0
    g18: LineSegment StartX=-40 StartY=-24.5 StartZ=0 EndX=-40 EndY=-19.5 EndZ=0
    g19: LineSegment StartX=-40 StartY=-19.5 StartZ=0 EndX=-31 EndY=-19.5 EndZ=0
    g20: LineSegment StartX=-31 StartY=-19.5 StartZ=0 EndX=-31 EndY=-14.5 EndZ=0
    g21: LineSegment StartX=-31 StartY=-14.5 StartZ=0 EndX=-40 EndY=-14.5 EndZ=0
  constraints (61):
    c: Coincident(g0,g1)
    c: Coincident(g1,g2)
    c: Coincident(g2,g3)
    c: Coincident(g3,g0)
    c: Horizontal(g0)
    c: Horizontal(g2)
    c: Vertical(g1)
    c: Vertical(g3)
    c: Distance(g-1,g0) = 15
    c: Distance(g-1,g2) = 29.5
    c: Distance(g-1,g3) = 40
    c: Distance(g-1,g1) = 80
    c: PointOnObject(g4,g-1)
    c: Diameter(g4) = 8.1
    c: Distance(g4,g-1) = 70
    c: Coincident(g5,g6)
    c: Coincident(g6,g7)
    c: Coincident(g7,g8)
    c: Coincident(g8,g9)
    c: Coincident(g9,g10)
    c: Coincident(g10,g5)
    c: Equal(g5, g6-g10) x5
    c: PointOnObject(g5,g11)
    c: PointOnObject(g6,g11)
    c: PointOnObject(g7,g11)
    c: PointOnObject(g8,g11)
    c: PointOnObject(g9,g11)
    c: PointOnObject(g10,g11)
    c: Coincident(g11,g-1)
    c: Distance(g-1,g10) = 6.4
    c: PointOnObject(g5,g-1)
    c: Coincident(g0,g12)
    c: Coincident(g13,g1)
    c: Diameter(g14) = 3
    c: Distance(g14,g13) = 15
    c: Distance(g14,g3) = 50
    c: Equal(g14,g15)
    c: Distance(g15,g13) = 15
    c: Distance(g15,g3) = 100
    c: Horizontal(g13)
    c: Coincident(g13,g16)
    c: Vertical(g16)
    c: Coincident(g16,g17)
    c: Horizontal(g17)
    c: Coincident(g17,g18)
    c: PointOnObject(g18,g3)
    c: Vertical(g18)
    c: Coincident(g18,g19)
    c: Horizontal(g19)
    c: Coincident(g19,g20)
    c: Coincident(g20,g21)
    c: Coincident(g21,g12)
    c: Horizontal(g21)
    c: Vertical(g20)
    c: Distance(g20) = 5
    c: Distance(g18) = 5
    c: Distance(g16) = 5
    c: Distance(g17) = 9
    c: Equal(g17,g19)
    c: Vertical(g12)
    c: Distance(g0,g2) = 44.5
FEATURE [PartDesign::Pad] Pad025
  Length = 9
  Length2 = 100
  Placement = pos=(0,0,0) rot=(0.57735,0.57735,0.57735;2.0944rad)
  Profile = -> Sketch048
  Type = 0
FEATURE [PartDesign::Body] endstueck
  Group = -> [Sketch048,Pad025]
  Origin = -> Origin029
  Placement = pos=(-214,135,29.5) rot=(0,0,1;3.14159rad)
  Tip = -> Pad025
FEATURE [PartDesign::ShapeBinder] CopyPad025
  Placement = pos=(0,0,0) rot=(0.57735,0.57735,0.57735;2.0944rad)
  TraceSupport = false
FEATURE [Sketcher::SketchObject] Sketch049
  MapMode = 5
  Placement = pos=(-1.1e-14,-25,5.5e-15) rot=(-0.57735,-0.57735,0.57735;4.18879rad)
  Support = -> [CopyPad025]
  sketch-geometry (11):
    g0: LineSegment StartX=24.5 StartY=9 StartZ=0 EndX=29.5 EndY=9 EndZ=0
    g1: LineSegment StartX=29.5 StartY=9 StartZ=0 EndX=29.5 EndY=-30 EndZ=0
    g2: LineSegment StartX=29.5 StartY=-30 StartZ=0 EndX=9.5 EndY=-30 EndZ=0
    g3: LineSegment StartX=9.5 StartY=-30 StartZ=0 EndX=9.5 EndY=0 EndZ=0
    g4: LineSegment StartX=24.5 StartY=0 StartZ=0 EndX=24.5 EndY=9 EndZ=0
    g5: Circle CenterX=14.5 CenterY=-15 CenterZ=0 NormalX=0 NormalY=0 NormalZ=1 AngleXU=0 Radius=1.5
    g6: LineSegment StartX=9.5 StartY=0 StartZ=0 EndX=14.5 EndY=0 EndZ=0
    g7: LineSegment StartX=14.5 StartY=0 StartZ=0 EndX=14.5 EndY=9 EndZ=0
    g8: LineSegment StartX=14.5 StartY=9 StartZ=0 EndX=19.5 EndY=9 EndZ=0
    g9: LineSegment StartX=19.5 StartY=9 StartZ=0 EndX=19.5 EndY=0 EndZ=0
    g10: LineSegment StartX=19.5 StartY=0 StartZ=0 EndX=24.5 EndY=0 EndZ=0
  constraints (33):
    c: Coincident(g0,g1)
    c: Vertical(g1)
    c: Coincident(g1,g2)
    c: Horizontal(g2)
    c: Coincident(g2,g3)
    c: PointOnObject(g3,g-1)
    c: Vertical(g3)
    c: PointOnObject(g4,g-1)
    c: Vertical(g4)
    c: Coincident(g4,g0)
    c: Horizontal(g0)
    c: Distance(g0) = 5
    c: Distance(g4) = 9
    c: Distance(g0,g-2) = 29.5
    c: Distance(g3) = 30
    c: Diameter(g5) = 3
    c: Distance(g5,g-1) = 15
    c: Distance(g5,g1) = 15
    c: Coincident(g3,g6)
    c: PointOnObject(g6,g-1)
    c: Coincident(g6,g7)
    c: Vertical(g7)
    c: Coincident(g7,g8)
    c: Horizontal(g8)
    c: Coincident(g8,g9)
    c: Vertical(g9)
    c: Coincident(g9,g10)
    c: Coincident(g10,g4)
    c: Distance(g10) = 5
    c: Distance(g8) = 5
    c: Equal(g4,g9)
    c: Equal(g9,g7)
    c: Distance(g6) = 5
FEATURE [PartDesign::Pad] Pad026
  Length = 9
  Length2 = 100
  Placement = pos=(0,0,0) rot=(0.57735,0.57735,0.57735;2.0944rad)
  Profile = -> Sketch049
  Type = 0
FEATURE [PartDesign::Body] endstueck_seite
  Group = -> [CopyPad025,Sketch049,Pad026]
  Origin = -> Origin030
  Placement = pos=(-214,141,29.5) rot=(0,0,1;3.14159rad)
  Tip = -> Pad026
FEATURE [App::Part] motor_kasten_horiz
  Group = -> [LCS_1,Body017,Body016,Body015,Body014,endstueck,endstueck_seite]
  Origin = -> Origin019
FEATURE [Sketcher::SketchObject] Sketch050
  MapMode = 5
  Support = -> [XY_Plane031]
  sketch-geometry (1):
    g0: Circle CenterX=0 CenterY=0 CenterZ=0 NormalX=0 NormalY=0 NormalZ=1 AngleXU=0 Radius=4
  constraints (2):
    c: Coincident(g0,g-1)
    c: Diameter(g0) = 8
FEATURE [PartDesign::Pad] Pad027
  Length = 198
  Length2 = 100
  Profile = -> Sketch050
  Type = 0
FEATURE [PartDesign::Body] Body026  label="fuehrung-vert"
  Group = -> [Sketch050,Pad027]
  Origin = -> Origin031
  Placement = pos=(145,100,56) rot=(0,0,1;0rad)
  Tip = -> Pad027
FEATURE [App::DocumentObjectGroup] Parts
FEATURE [PartDesign::CoordinateSystem] LCS_0
  AttacherType = Attacher::AttachEngine3D
  MapMode = 2
  Support = -> [X_Axis032]
FEATURE [App::DocumentObjectGroup] Constraints
FEATURE [App::FeaturePython] Variables  # WARN: FeaturePython — macro-defined, semantics opaque (R4)
FEATURE [PartDesign::FeatureBase] Clone003
  BaseFeature = -> Body020
  Placement = pos=(100,135,29.5) rot=(0,0,1;0rad)
FEATURE [PartDesign::Body] Body028
  BaseFeature = -> Body020
  Group = -> [Clone003]
  Origin = -> Origin034
  Placement = pos=(186,270,0) rot=(0,0,1;3.14159rad)
  Tip = -> Clone003
FEATURE [Sketcher::SketchObject] Sketch051
  MapMode = 5
  Placement = pos=(71,1.6908e-12,-5.11e-14) rot=(0.57735,0.57735,0.57735;2.0944rad)
  Support = -> [Pad022]
  sketch-geometry (1):
    g0: Circle CenterX=35 CenterY=45 CenterZ=0 NormalX=0 NormalY=0 NormalZ=1 AngleXU=0 Radius=4.05
  constraints (3):
    c: Radius(g0) = 4.05
    c: Distance(g0,g-2) = 35
    c: Distance(g0,g-1) = 45
FEATURE [PartDesign::Pocket] Pocket015
  BaseFeature = -> Pad022
  Length = 5
  Length2 = 100
  Placement = pos=(0,0,0) rot=(0.57735,0.57735,0.57735;2.0944rad)
  Profile = -> Sketch051
  Type = 0
FEATURE [PartDesign::Body] Body022  label="tischplatte"
  Group = -> [CopyPocket014001,Sketch045,Pad022,Sketch051,Pocket015]
  Origin = -> Origin024
  Placement = pos=(100,135,29.5) rot=(0,0,1;0rad)
  Tip = -> Pocket015
FEATURE [Sketcher::SketchObject] Sketch052
  MapMode = 5
  Support = -> [XY_Plane035]
  sketch-geometry (25):
    g0: Circle CenterX=-3 CenterY=4 CenterZ=0 NormalX=0 NormalY=0 NormalZ=1 AngleXU=0 Radius=27.5
    g1: Circle [constr] CenterX=-3 CenterY=4 CenterZ=0 NormalX=0 NormalY=0 NormalZ=1 AngleXU=0 Radius=42.5
    g2: LineSegment StartX=-67 StartY=-60 StartZ=0 EndX=-67 EndY=-21.7168 EndZ=0
    g3: LineSegment StartX=-67 StartY=-21.7168 StartZ=0 EndX=-45.3113 EndY=3.55e-14 EndZ=0
    g4: LineSegment [constr] StartX=-67 StartY=-60 StartZ=0 EndX=60 EndY=-60 EndZ=0
    g5: LineSegment StartX=60 StartY=-60 StartZ=0 EndX=60 EndY=-21.7507 EndZ=0
    g6: LineSegment StartX=60 StartY=-21.7507 StartZ=0 EndX=39.3113 EndY=7.1e-15 EndZ=0
    g7: LineSegment StartX=51.4 StartY=-38.695 StartZ=0 EndX=51.4 EndY=-31.305 EndZ=0
    g8: LineSegment StartX=51.4 StartY=-31.305 StartZ=0 EndX=45 EndY=-27.6099 EndZ=0
    g9: LineSegment StartX=45 StartY=-27.6099 StartZ=0 EndX=38.6 EndY=-31.305 EndZ=0
    g10: LineSegment StartX=38.6 StartY=-31.305 StartZ=0 EndX=38.6 EndY=-38.695 EndZ=0
    g11: LineSegment StartX=38.6 StartY=-38.695 StartZ=0 EndX=45 EndY=-42.3901 EndZ=0
    g12: LineSegment StartX=45 StartY=-42.3901 StartZ=0 EndX=51.4 EndY=-38.695 EndZ=0
    g13: Circle [constr] CenterX=45 CenterY=-35 CenterZ=0 NormalX=0 NormalY=0 NormalZ=1 AngleXU=0 Radius=7.39008
    g14: ArcOfCircle CenterX=-3 CenterY=4 CenterZ=0 NormalX=0 NormalY=0 NormalZ=1 AngleXU=0 Radius=42.5 StartAngle=6.18893 EndAngle=9.51904
    g15: Circle CenterX=-52 CenterY=-35 CenterZ=0 NormalX=0 NormalY=0 NormalZ=1 AngleXU=0 Radius=4.15
    g16: LineSegment StartX=-67 StartY=-60 StartZ=0 EndX=-37.5 EndY=-60 EndZ=0
    g17: LineSegment StartX=-37.5 StartY=-60 StartZ=0 EndX=-37.5 EndY=-51 EndZ=0
    g18: LineSegment StartX=-37.5 StartY=-51 StartZ=0 EndX=-12.5 EndY=-51 EndZ=0
    g19: LineSegment StartX=-12.5 StartY=-51 StartZ=0 EndX=-12.5 EndY=-60 EndZ=0
    g20: LineSegment StartX=-12.5 StartY=-60 StartZ=0 EndX=12.5 EndY=-60 EndZ=0
    g21: LineSegment StartX=12.5 StartY=-60 StartZ=0 EndX=12.5 EndY=-51 EndZ=0
    g22: LineSegment StartX=12.5 StartY=-51 StartZ=0 EndX=37.5 EndY=-51 EndZ=0
    g23: LineSegment StartX=37.5 StartY=-51 StartZ=0 EndX=37.5 EndY=-60 EndZ=0
    g24: LineSegment StartX=37.5 StartY=-60 StartZ=0 EndX=60 EndY=-60 EndZ=0
  constraints (70):
    c: Coincident(g0,g1)
    c: Distance(g0,g-2) = 3
    c: Distance(g0,g-1) = 4
    c: Diameter(g0) = 55
    c: Diameter(g1) = 85
    c: Vertical(g2)
    c: Coincident(g2,g3)
    c: PointOnObject(g3,g1)
    c: Horizontal(g4)
    c: Coincident(g4,g5)
    c: Vertical(g5)
    c: Coincident(g5,g6)
    c: Coincident(g7,g8)
    c: Coincident(g8,g9)
    c: Coincident(g9,g10)
    c: Coincident(g10,g11)
    c: Coincident(g11,g12)
    c: Coincident(g12,g7)
    c: Equal(g7, g8-g12) x5
    c: PointOnObject(g7,g13)
    c: PointOnObject(g8,g13)
    c: PointOnObject(g9,g13)
    c: PointOnObject(g10,g13)
    c: PointOnObject(g11,g13)
    c: PointOnObject(g12,g13)
    c: Distance(g13,g8) = 6.4
    c: Distance(g13,g-1) = 35
    c: Distance(g13,g-2) = 45
    c: Distance(g13,g5) = 15
    c: Coincident(g14,g0)
    c: Coincident(g14,g6)
    c: Coincident(g14,g3)
    c: Diameter(g15) = 8.3
    c: Distance(g15,g-1) = 35
    c: Distance(g15,g-2) = 52
    c: PointOnObject(g6,g-1)
    c: PointOnObject(g3,g-1)
    c: Distance(g15,g2) = 15
    c: Distance(g15,g4) = 25
    c: Vertical(g7)
    c: Distance(g13,g6) = 20
    c: Distance(g15,g3) = 20
    c: Distance(g13,g4) = 25
    c: Coincident(g16,g2)
    c: PointOnObject(g16,g4)
    c: PointOnObject(g2,g4)
    c: Coincident(g16,g17)
    c: Vertical(g17)
    c: Coincident(g17,g18)
    c: Horizontal(g18)
    c: Coincident(g18,g19)
    c: PointOnObject(g19,g4)
    c: Coincident(g19,g20)
    c: Coincident(g20,g21)
    c: Coincident(g21,g22)
    c: Horizontal(g22)
    c: Coincident(g22,g23)
    c: Vertical(g23)
    c: Coincident(g23,g24)
    c: Vertical(g19)
    c: Vertical(g21)
    c: Equal(g21,g19)
    c: Distance(g17) = 9
    c: Distance(g18) = 25
    c: Distance(g22) = 25
    c: Distance(g20) = 25
    c: Symmetric(g19,g20,g-2)
    c: Coincident(g24,g5)
    c: Horizontal(g24)
    c: DistanceX(g4,g4) = 127
FEATURE [PartDesign::ShapeBinder] CopyPocket016
  TraceSupport = false
FEATURE [Sketcher::SketchObject] Sketch054
  MapMode = 5
  Placement = pos=(0,-60,0) rot=(1,0,0;1.5708rad)
  Support = -> [CopyPocket016]
  sketch-geometry (32):
    g0: LineSegment StartX=-67 StartY=0 StartZ=0 EndX=-37.5 EndY=0 EndZ=0
    g1: LineSegment StartX=-37.5 StartY=0 StartZ=0 EndX=-37.5 EndY=15 EndZ=0
    g2: LineSegment StartX=-37.5 StartY=15 StartZ=0 EndX=-12.5 EndY=15 EndZ=0
    g3: LineSegment StartX=-12.5 StartY=15 StartZ=0 EndX=-12.5 EndY=0 EndZ=0
    g4: LineSegment StartX=-12.5 StartY=0 StartZ=0 EndX=12.5 EndY=0 EndZ=0
    g5: LineSegment StartX=12.5 StartY=0 StartZ=0 EndX=12.5 EndY=15 EndZ=0
    g6: LineSegment StartX=12.5 StartY=15 StartZ=0 EndX=37.5 EndY=15 EndZ=0
    g7: LineSegment StartX=37.5 StartY=15 StartZ=0 EndX=37.5 EndY=0 EndZ=0
    g8: LineSegment StartX=37.5 StartY=0 StartZ=0 EndX=60 EndY=0 EndZ=0
    g9: LineSegment StartX=60 StartY=0 StartZ=0 EndX=60 EndY=-80 EndZ=0
    g10: LineSegment [constr] StartX=60 StartY=-80 StartZ=0 EndX=30 EndY=-80 EndZ=0
    g11: LineSegment StartX=30 StartY=-80 StartZ=0 EndX=-37 EndY=-29 EndZ=0
    g12: LineSegment [constr] StartX=-37 StartY=-29 StartZ=0 EndX=-67 EndY=-29 EndZ=0
    g13: LineSegment StartX=-67 StartY=-29 StartZ=0 EndX=-67 EndY=0 EndZ=0
    g14: LineSegment StartX=30 StartY=-80 StartZ=0 EndX=40 EndY=-80 EndZ=0
    g15: LineSegment StartX=40 StartY=-80 StartZ=0 EndX=40 EndY=-65 EndZ=0
    g16: LineSegment StartX=55 StartY=-65 StartZ=0 EndX=55 EndY=-80 EndZ=0
    g17: LineSegment StartX=55 StartY=-80 StartZ=0 EndX=60 EndY=-80 EndZ=0
    g18: LineSegment StartX=40 StartY=-65 StartZ=0 EndX=45 EndY=-65 EndZ=0
    g19: LineSegment StartX=45 StartY=-65 StartZ=0 EndX=45 EndY=-80 EndZ=0
    g20: LineSegment StartX=45 StartY=-80 StartZ=0 EndX=50 EndY=-80 EndZ=0
    g21: LineSegment StartX=50 StartY=-80 StartZ=0 EndX=50 EndY=-65 EndZ=0
    g22: LineSegment StartX=50 StartY=-65 StartZ=0 EndX=55 EndY=-65 EndZ=0
    g23: LineSegment StartX=-67 StartY=-29 StartZ=0 EndX=-62 EndY=-29 EndZ=0
    g24: LineSegment StartX=-62 StartY=-29 StartZ=0 EndX=-62 EndY=-14 EndZ=0
    g25: LineSegment StartX=-62 StartY=-14 StartZ=0 EndX=-57 EndY=-14 EndZ=0
    g26: LineSegment StartX=-57 StartY=-14 StartZ=0 EndX=-57 EndY=-29 EndZ=0
    g27: LineSegment StartX=-57 StartY=-29 StartZ=0 EndX=-52 EndY=-29 EndZ=0
    g28: LineSegment StartX=-52 StartY=-29 StartZ=0 EndX=-52 EndY=-14 EndZ=0
    g29: LineSegment StartX=-52 StartY=-14 StartZ=0 EndX=-47 EndY=-14 EndZ=0
    g30: LineSegment StartX=-47 StartY=-14 StartZ=0 EndX=-47 EndY=-29 EndZ=0
    g31: LineSegment StartX=-47 StartY=-29 StartZ=0 EndX=-37 EndY=-29 EndZ=0
  constraints (93):
    c: PointOnObject(g0,g-1)
    c: PointOnObject(g0,g-1)
    c: Coincident(g0,g1)
    c: Coincident(g1,g2)
    c: Horizontal(g2)
    c: Coincident(g2,g3)
    c: Vertical(g3)
    c: Coincident(g3,g4)
    c: Coincident(g4,g5)
    c: Vertical(g5)
    c: Coincident(g5,g6)
    c: Coincident(g6,g7)
    c: Vertical(g7)
    c: Coincident(g7,g8)
    c: Coincident(g8,g9)
    c: Vertical(g9)
    c: Coincident(g9,g10)
    c: Horizontal(g10)
    c: Coincident(g10,g11)
    c: Coincident(g11,g12)
    c: Horizontal(g12)
    c: Coincident(g12,g13)
    c: Coincident(g13,g0)
    c: Vertical(g13)
    c: Vertical(g1)
    c: Equal(g1,g3)
    c: Distance(g1) = 15
    c: Distance(g2) = 25
    c: Horizontal(g6)
    c: Equal(g3,g5)
    c: Equal(g5,g7)
    c: Distance(g6) = 25
    c: Distance(g4) = 25
    c: Horizontal(g8)
    c: Distance(g8,g-2) = 60
    c: Distance(g0,g-2) = 67
    c: Symmetric(g3,g4,g-1)
    c: Distance(g13) = 29
    c: Distance(g12) = 30
    c: Distance(g9) = 80
    c: Distance(g10) = 30
    c: Coincident(g11,g14)
    c: PointOnObject(g14,g10)
    c: Coincident(g14,g15)
    c: PointOnObject(g16,g10)
    c: Coincident(g16,g17)
    c: Coincident(g17,g9)
    c: Vertical(g15)
    c: Vertical(g16)
    c: Distance(g15) = 15
    c: Coincident(g15,g18)
    c: Horizontal(g18)
    c: Coincident(g18,g19)
    c: PointOnObject(g19,g10)
    c: Coincident(g19,g20)
    c: PointOnObject(g20,g10)
    c: Coincident(g20,g21)
    c: Vertical(g21)
    c: Coincident(g21,g22)
    c: Horizontal(g22)
    c: Vertical(g19)
    c: Coincident(g16,g22)
    c: Equal(g15,g21)
    c: Distance(g18) = 5
    c: Distance(g20) = 5
    c: Distance(g22) = 5
    c: Distance(g17) = 5
    c: Coincident(g13,g23)
    c: Horizontal(g23)
    c: Coincident(g23,g24)
    c: Coincident(g24,g25)
    c: Horizontal(g25)
    c: Coincident(g25,g26)
    c: PointOnObject(g26,g12)
    c: Coincident(g26,g27)
    c: PointOnObject(g27,g12)
    c: Coincident(g27,g28)
    c: Vertical(g28)
    c: Coincident(g28,g29)
    c: Horizontal(g29)
    c: Coincident(g29,g30)
    c: PointOnObject(g30,g12)
    c: Vertical(g30)
    c: Coincident(g30,g31)
    c: Coincident(g31,g11)
    c: Vertical(g24)
    c: Vertical(g26)
    c: Equal(g26,g28)
    c: DistanceY(g24,g24) = 15
    c: Equal(g25,g29)
    c: DistanceX(g29,g29) = 5
    c: DistanceX(g27,g27) = 5
    c: DistanceX(g23,g23) = 5
FEATURE [PartDesign::Pad] Pad029
  Length = 9
  Length2 = 100
  Profile = -> Sketch054
  Reversed = true
  Type = 0
FEATURE [PartDesign::Body] Body030  label="Wand v fixierung"
  Group = -> [CopyPocket016,Sketch054,Pad029]
  Origin = -> Origin036
  Placement = pos=(100,135,190) rot=(0,0,1;0rad)
  Tip = -> Pad029
FEATURE [PartDesign::CoordinateSystem] LCS_1003
  AttacherType = Attacher::AttachEngine3D
  MapMode = 2
  Support = -> [X_Axis037]
FEATURE [App::Part] glas
  Group = -> [LCS_1003,Body]
  Origin = -> Origin037
FEATURE [PartDesign::CoordinateSystem] LCS_1004
  AttacherType = Attacher::AttachEngine3D
  MapMode = 2
  Support = -> [X_Axis038]
FEATURE [App::Part] motoren
  Group = -> [LCS_1004,Body005,Body007,Body012,Body013,Body025,Body026]
  Origin = -> Origin038
FEATURE [TechDraw::DrawViewDimension] Dimension005
  Arbitrary = false
  FormatSpec = %.3f
  Inverted = false
  LockPosition = false
  MeasureType = 1
  OverTolerance = 0
  References2D = -> [ProjItem]
  Rotation = 0
  ScaleType = 0
  TheoreticalExact = false
  Type = 1
  UnderTolerance = 0
  X = -0.358974
  Y = 44.5064
FEATURE [TechDraw::DrawViewDimension] Dimension006
  Arbitrary = false
  FormatSpec = %.3f
  Inverted = false
  LockPosition = false
  MeasureType = 1
  OverTolerance = 0
  References2D = -> [ProjItem]
  Rotation = 0
  ScaleType = 0
  TheoreticalExact = false
  Type = 1
  UnderTolerance = 0
  X = -0.346154
  Y = 38.7308
FEATURE [TechDraw::DrawPage] Page
  KeepUpdated = true
  NextBalloonIndex = 1
  ProjectionType = 0
  Template = -> Template
  Views = -> [ProjGroup,Dimension,Dimension001,Dimension002,Dimension003,Dimension004,Dimension005,Dimension006]
FEATURE [Sketcher::SketchObject] Sketch055
  MapMode = 5
  Placement = pos=(0,0,0) rot=(0.57735,0.57735,-0.57735;4.18879rad)
  Support = -> [Pad020]
  sketch-geometry (7):
    g0: LineSegment StartX=7.39008 StartY=5.06e-14 StartZ=0 EndX=3.69504 EndY=6.4 EndZ=0
    g1: LineSegment StartX=3.69504 StartY=6.4 StartZ=0 EndX=-3.69504 EndY=6.4 EndZ=0
    g2: LineSegment StartX=-3.69504 StartY=6.4 StartZ=0 EndX=-7.39008 EndY=-5.24e-14 EndZ=0
    g3: LineSegment StartX=-7.39008 StartY=-5.24e-14 StartZ=0 EndX=-3.69504 EndY=-6.4 EndZ=0
    g4: LineSegment StartX=-3.69504 StartY=-6.4 StartZ=0 EndX=3.69504 EndY=-6.4 EndZ=0
    g5: LineSegment StartX=3.69504 StartY=-6.4 StartZ=0 EndX=7.39008 EndY=5.06e-14 EndZ=0
    g6: Circle [constr] CenterX=0 CenterY=0 CenterZ=0 NormalX=0 NormalY=0 NormalZ=1 AngleXU=0 Radius=7.39008
  constraints (16):
    c: Coincident(g0,g1)
    c: Coincident(g1,g2)
    c: Coincident(g2,g3)
    c: Coincident(g3,g4)
    c: Coincident(g4,g5)
    c: Coincident(g5,g0)
    c: Equal(g0, g1-g5) x5
    c: PointOnObject(g0,g6)
    c: PointOnObject(g1,g6)
    c: PointOnObject(g2,g6)
    c: PointOnObject(g3,g6)
    c: PointOnObject(g4,g6)
    c: PointOnObject(g5,g6)
    c: Coincident(g6,g-1)
    c: Distance(g-1,g0) = 6.4
    c: Horizontal(g4)
FEATURE [PartDesign::Pocket] Pocket017
  BaseFeature = -> Pad020
  Length = 8
  Length2 = 100
  Placement = pos=(0,0,0) rot=(0.57735,0.57735,0.57735;2.0944rad)
  Profile = -> Sketch055
  Type = 0
FEATURE [PartDesign::Body] Body018
  Group = -> [Sketch042,Pad020,Sketch055,Pocket017]
  Origin = -> Origin018
  Placement = pos=(100,135,29.5) rot=(0,0,1;0rad)
  Tip = -> Pocket017
FEATURE [PartDesign::FeatureBase] Clone
  BaseFeature = -> Body018
  Placement = pos=(100,135,29.5) rot=(0,0,1;0rad)
FEATURE [PartDesign::Body] Body027
  BaseFeature = -> Body018
  Group = -> [Clone]
  Origin = -> Origin033
  Placement = pos=(186,270,0) rot=(0,0,1;3.14159rad)
  Tip = -> Clone
FEATURE [App::Part] fuehrung_horiz_gewinde  label="tisch"
  Group = -> [LCS_1001,Body024,Body020,Body018,Body027,Body028,Body023,Body022]
  Origin = -> Origin023
FEATURE [PartDesign::ShapeBinder] CopyPad029
  TraceSupport = false
FEATURE [Sketcher::SketchObject] Sketch056
  MapMode = 5
  Placement = pos=(0,-1.76e-14,-80) rot=(1,0,0;3.14159rad)
  Support = -> [CopyPad029]
  sketch-geometry (25):
    g0: LineSegment [constr] StartX=60 StartY=22 StartZ=0 EndX=30 EndY=22 EndZ=0
    g1: LineSegment [constr] StartX=30 StartY=22 StartZ=0 EndX=30 EndY=60 EndZ=0
    g2: LineSegment [constr] StartX=30 StartY=60 StartZ=0 EndX=60 EndY=60 EndZ=0
    g3: LineSegment [constr] StartX=60 StartY=60 StartZ=0 EndX=60 EndY=22 EndZ=0
    g4: LineSegment StartX=60 StartY=35 StartZ=0 EndX=60 EndY=51 EndZ=0
    g5: LineSegment StartX=60 StartY=51 StartZ=0 EndX=55 EndY=51 EndZ=0
    g6: LineSegment StartX=55 StartY=51 StartZ=0 EndX=55 EndY=60 EndZ=0
    g7: LineSegment StartX=55 StartY=60 StartZ=0 EndX=50 EndY=60 EndZ=0
    g8: LineSegment StartX=50 StartY=60 StartZ=0 EndX=50 EndY=51 EndZ=0
    g9: LineSegment StartX=50 StartY=51 StartZ=0 EndX=45 EndY=51 EndZ=0
    g10: LineSegment StartX=45 StartY=51 StartZ=0 EndX=45 EndY=60 EndZ=0
    g11: LineSegment StartX=45 StartY=60 StartZ=0 EndX=40 EndY=60 EndZ=0
    g12: LineSegment StartX=40 StartY=60 StartZ=0 EndX=40 EndY=51 EndZ=0
    g13: LineSegment StartX=40 StartY=51 StartZ=0 EndX=30 EndY=51 EndZ=0
    g14: LineSegment StartX=47 StartY=22 StartZ=0 EndX=43 EndY=22 EndZ=0
    g15: LineSegment StartX=30 StartY=35 StartZ=0 EndX=30 EndY=51 EndZ=0
    g16: ArcOfCircle CenterX=43 CenterY=35 CenterZ=0 NormalX=0 NormalY=0 NormalZ=1 AngleXU=0 Radius=13 StartAngle=3.14159 EndAngle=4.71239
    g17: ArcOfCircle CenterX=47 CenterY=35 CenterZ=0 NormalX=0 NormalY=0 NormalZ=1 AngleXU=0 Radius=13 StartAngle=4.71239 EndAngle=6.28319
    g18: LineSegment StartX=45 StartY=42.3901 StartZ=0 EndX=38.6 EndY=38.695 EndZ=0
    g19: LineSegment StartX=38.6 StartY=38.695 StartZ=0 EndX=38.6 EndY=31.305 EndZ=0
    g20: LineSegment StartX=38.6 StartY=31.305 StartZ=0 EndX=45 EndY=27.6099 EndZ=0
    g21: LineSegment StartX=45 StartY=27.6099 StartZ=0 EndX=51.4 EndY=31.305 EndZ=0
    g22: LineSegment StartX=51.4 StartY=31.305 StartZ=0 EndX=51.4 EndY=38.695 EndZ=0
    g23: LineSegment StartX=51.4 StartY=38.695 StartZ=0 EndX=45 EndY=42.3901 EndZ=0
    g24: Circle [constr] CenterX=45 CenterY=35 CenterZ=0 NormalX=0 NormalY=0 NormalZ=1 AngleXU=0 Radius=7.39008
  constraints (69):
    c: Coincident(g0,g1)
    c: Coincident(g1,g2)
    c: Coincident(g2,g3)
    c: Coincident(g3,g0)
    c: Horizontal(g0)
    c: Horizontal(g2)
    c: Vertical(g1)
    c: Vertical(g3)
    c: Vertical(g4)
    c: Coincident(g4,g5)
    c: Horizontal(g5)
    c: Coincident(g5,g6)
    c: Coincident(g6,g7)
    c: PointOnObject(g7,g2)
    c: Horizontal(g7)
    c: Coincident(g7,g8)
    c: Coincident(g8,g9)
    c: Horizontal(g9)
    c: Coincident(g9,g10)
    c: Vertical(g10)
    c: Coincident(g10,g11)
    c: PointOnObject(g11,g2)
    c: Coincident(g11,g12)
    c: Vertical(g12)
    c: Coincident(g12,g13)
    c: PointOnObject(g13,g1)
    c: Horizontal(g13)
    c: Vertical(g8)
    c: Vertical(g6)
    c: Coincident(g15,g13)
    c: Tangent(g14,g16) = 1.5708
    c: Tangent(g15,g16) = 1.5708
    c: Vertical(g15)
    c: Horizontal(g14)
    c: Tangent(g4,g17) = -1.5708
    c: Tangent(g14,g17) = 1.5708
    c: Distance(g6) = 9
    c: Equal(g6,g10)
    c: Equal(g6,g8)
    c: Equal(g6,g12)
    c: Distance(g5) = 5
    c: Distance(g7) = 5
    c: Distance(g9) = 5
    c: Distance(g11) = 5
    c: Coincident(g18,g19)
    c: Coincident(g19,g20)
    c: Coincident(g20,g21)
    c: Coincident(g21,g22)
    c: Coincident(g22,g23)
    c: Coincident(g23,g18)
    c: Equal(g18, g19-g23) x5
    c: PointOnObject(g18,g24)
    c: PointOnObject(g19,g24)
    c: PointOnObject(g20,g24)
    c: PointOnObject(g21,g24)
    c: PointOnObject(g22,g24)
    c: PointOnObject(g23,g24)
    c: Distance(g24,g19) = 6.4
    c: Vertical(g22)
    c: DistanceX(g13,g4) = 30
    c: Distance(g24,g4) = 15
    c: Distance(g24,g2) = 25
    c: PointOnObject(g4,g3)
    c: Distance(g24,g-2) = 45
    c: PointOnObject(g14,g0)
    c: Distance(g24,g-1) = 35
    c: Equal(g17,g16)
    c: Radius(g17) = 13
    c: Distance(g24,g14) = 13
FEATURE [PartDesign::Pad] Pad030
  Length = 15
  Length2 = 100
  Profile = -> Sketch056
  Reversed = true
  Type = 0
FEATURE [PartDesign::Body] Body031
  Group = -> [CopyPad029,Sketch056,Pad030]
  Origin = -> Origin039
  Placement = pos=(100,135,190) rot=(0,0,1;0rad)
  Tip = -> Pad030
FEATURE [PartDesign::Pad] Pad031
  Length = 15
  Length2 = 100
  Profile = -> Sketch052
  Type = 0
FEATURE [PartDesign::Plane] DatumPlane001
  Length = 60
  MapMode = 5
  Placement = pos=(0,0,0) rot=(1,0,0;3.14159rad)
  ResizeMode = 0
  Support = -> [Pad031]
  Width = 60
FEATURE [Sketcher::SketchObject] Sketch057
  MapMode = 5
  Placement = pos=(0,0,0) rot=(1,0,0;3.14159rad)
  Support = -> [DatumPlane001]
  sketch-geometry (8):
    g0: LineSegment StartX=-45.6 StartY=31.305 StartZ=0 EndX=-45.6 EndY=38.695 EndZ=0
    g1: LineSegment StartX=-45.6 StartY=38.695 StartZ=0 EndX=-52 EndY=42.3901 EndZ=0
    g2: LineSegment StartX=-52 StartY=42.3901 StartZ=0 EndX=-58.4 EndY=38.695 EndZ=0
    g3: LineSegment StartX=-58.4 StartY=38.695 StartZ=0 EndX=-58.4 EndY=31.305 EndZ=0
    g4: LineSegment StartX=-58.4 StartY=31.305 StartZ=0 EndX=-52 EndY=27.6099 EndZ=0
    g5: LineSegment StartX=-52 StartY=27.6099 StartZ=0 EndX=-45.6 EndY=31.305 EndZ=0
    g6: Circle [constr] CenterX=-52 CenterY=35 CenterZ=0 NormalX=0 NormalY=0 NormalZ=1 AngleXU=0 Radius=7.39008
    g7: Circle [constr] CenterX=-52 CenterY=35 CenterZ=0 NormalX=0 NormalY=0 NormalZ=1 AngleXU=0 Radius=6.4
  constraints (19):
    c: Coincident(g0,g1)
    c: Coincident(g1,g2)
    c: Coincident(g2,g3)
    c: Coincident(g3,g4)
    c: Coincident(g4,g5)
    c: Coincident(g5,g0)
    c: Equal(g0, g1-g5) x5
    c: PointOnObject(g0,g6)
    c: PointOnObject(g1,g6)
    c: PointOnObject(g2,g6)
    c: PointOnObject(g3,g6)
    c: PointOnObject(g4,g6)
    c: PointOnObject(g5,g6)
    c: Coincident(g7,g6)
    c: Tangent(g7,g1)
    c: Radius(g7) = 6.4
    c: Vertical(g3)
    c: Distance(g6,g-2) = 52
    c: Distance(g6,g-1) = 35
FEATURE [PartDesign::Pocket] Pocket018
  BaseFeature = -> Pad031
  Length = 8
  Length2 = 100
  Profile = -> Sketch057
  Type = 0
FEATURE [PartDesign::Body] Body029
  Group = -> [Sketch052,Pad031,DatumPlane001,Sketch057,Pocket018]
  Origin = -> Origin035
  Placement = pos=(100,135,190) rot=(0,0,1;0rad)
  Tip = -> Pocket018
FEATURE [PartDesign::ShapeBinder] CopyPad029001
  TraceSupport = false
FEATURE [PartDesign::Plane] DatumPlane002
  Length = 60
  MapMode = 5
  Placement = pos=(0,-6.4e-15,-29) rot=(1,0,0;3.14159rad)
  ResizeMode = 0
  Support = -> [CopyPad029001]
  Width = 60
FEATURE [Sketcher::SketchObject] Sketch058
  MapMode = 5
  Placement = pos=(0,-6.4e-15,-29) rot=(1,0,0;3.14159rad)
  Support = -> [DatumPlane002]
  sketch-geometry (25):
    g0: LineSegment [constr] StartX=-67 StartY=60 StartZ=0 EndX=-37 EndY=60 EndZ=0
    g1: LineSegment [constr] StartX=-37 StartY=60 StartZ=0 EndX=-37 EndY=35 EndZ=0
    g2: LineSegment StartX=-50 StartY=22 StartZ=0 EndX=-54 EndY=22 EndZ=0
    g3: LineSegment [constr] StartX=-67 StartY=35 StartZ=0 EndX=-67 EndY=60 EndZ=0
    g4: ArcOfCircle CenterX=-54 CenterY=35 CenterZ=0 NormalX=0 NormalY=0 NormalZ=1 AngleXU=0 Radius=13 StartAngle=3.14159 EndAngle=4.71239
    g5: ArcOfCircle CenterX=-50 CenterY=35 CenterZ=0 NormalX=0 NormalY=0 NormalZ=1 AngleXU=0 Radius=13 StartAngle=4.71239 EndAngle=6.28319
    g6: LineSegment StartX=-45.6 StartY=31.305 StartZ=0 EndX=-45.6 EndY=38.695 EndZ=0
    g7: LineSegment StartX=-45.6 StartY=38.695 StartZ=0 EndX=-52 EndY=42.3901 EndZ=0
    g8: LineSegment StartX=-52 StartY=42.3901 StartZ=0 EndX=-58.4 EndY=38.695 EndZ=0
    g9: LineSegment StartX=-58.4 StartY=38.695 StartZ=0 EndX=-58.4 EndY=31.305 EndZ=0
    g10: LineSegment StartX=-58.4 StartY=31.305 StartZ=0 EndX=-52 EndY=27.6099 EndZ=0
    g11: LineSegment StartX=-52 StartY=27.6099 StartZ=0 EndX=-45.6 EndY=31.305 EndZ=0
    g12: Circle [constr] CenterX=-52 CenterY=35 CenterZ=0 NormalX=0 NormalY=0 NormalZ=1 AngleXU=0 Radius=7.39008
    g13: Circle [constr] CenterX=-52 CenterY=35 CenterZ=0 NormalX=0 NormalY=0 NormalZ=1 AngleXU=0 Radius=6.4
    g14: LineSegment StartX=-67 StartY=35 StartZ=0 EndX=-67 EndY=51 EndZ=0
    g15: LineSegment StartX=-67 StartY=51 StartZ=0 EndX=-62 EndY=51 EndZ=0
    g16: LineSegment StartX=-57 StartY=51 StartZ=0 EndX=-52 EndY=51 EndZ=0
    g17: LineSegment StartX=-52 StartY=51 StartZ=0 EndX=-52 EndY=60 EndZ=0
    g18: LineSegment StartX=-52 StartY=60 StartZ=0 EndX=-47 EndY=60 EndZ=0
    g19: LineSegment StartX=-47 StartY=60 StartZ=0 EndX=-47 EndY=51 EndZ=0
    g20: LineSegment StartX=-47 StartY=51 StartZ=0 EndX=-37 EndY=51 EndZ=0
    g21: LineSegment StartX=-37 StartY=51 StartZ=0 EndX=-37 EndY=35 EndZ=0
    g22: LineSegment StartX=-62 StartY=60 StartZ=0 EndX=-62 EndY=51 EndZ=0
    g23: LineSegment StartX=-62 StartY=60 StartZ=0 EndX=-57 EndY=60 EndZ=0
    g24: LineSegment StartX=-57 StartY=60 StartZ=0 EndX=-57 EndY=51 EndZ=0
  constraints (71):
    c: Horizontal(g0)
    c: Horizontal(g2)
    c: Vertical(g1)
    c: Vertical(g3)
    c: DistanceX(g-2,g3) = -67
    c: Distance(g1,g3) = 30
    c: Distance(g3) = 25
    c: Equal(g3,g1)
    c: Radius(g5) = 13
    c: Coincident(g6,g7)
    c: Coincident(g7,g8)
    c: Coincident(g8,g9)
    c: Coincident(g9,g10)
    c: Coincident(g10,g11)
    c: Coincident(g11,g6)
    c: Equal(g6, g7-g11) x5
    c: PointOnObject(g6,g12)
    c: PointOnObject(g7,g12)
    c: PointOnObject(g8,g12)
    c: PointOnObject(g9,g12)
    c: PointOnObject(g10,g12)
    c: PointOnObject(g11,g12)
    c: Vertical(g9)
    c: Coincident(g13,g12)
    c: Tangent(g13,g7)
    c: Radius(g13) = 6.4
    c: DistanceY(g-1,g12) = 35
    c: DistanceX(g-2,g12) = -52
    c: Coincident(g14,g15)
    c: Horizontal(g15)
    c: Coincident(g16,g17)
    c: Coincident(g17,g18)
    c: Coincident(g18,g19)
    c: Coincident(g19,g20)
    c: Horizontal(g20)
    c: Coincident(g20,g21)
    c: Coincident(g21,g5)
    c: Equal(g19,g17)
    c: DistanceX(g18,g18) = 5
    c: Vertical(g19)
    c: Distance(g15) = 5
    c: Coincident(g1,g0)
    c: Coincident(g0,g3)
    c: Coincident(g5,g1)
    c: Coincident(g4,g14)
    c: Coincident(g4,g3)
    c: Coincident(g4,g2)
    c: Coincident(g2,g5)
    c: Vertical(g14)
    c: Vertical(g21)
    c: Vertical(g17)
    c: Coincident(g15,g22)
    c: Coincident(g22,g23)
    c: Coincident(g23,g24)
    c: Coincident(g24,g16)
    c: Vertical(g24)
    c: Vertical(g22)
    c: Horizontal(g23)
    c: Horizontal(g16)
    c: Horizontal(g18)
    c: Equal(g24,g22)
    c: Equal(g24,g17)
    c: Distance(g23) = 5
    c: Distance(g16) = 5
    c: Distance(g0,g14) = 9
    c: DistanceY(g-1,g0) = 60
    c: PointOnObject(g22,g0)
    c: Equal(g4,g5)
    c: DistanceY(g2,g5) = 13
    c: Distance(g4,g0) = 25
    c: Distance(g12,g2) = 13
FEATURE [PartDesign::Pad] Pad032
  Length = 15
  Length2 = 100
  Placement = pos=(0,-6e-15,-29) rot=(1,0,0;3.14159rad)
  Profile = -> Sketch058
  Reversed = true
  Type = 0
FEATURE [PartDesign::Body] Body032  label="Fixierung 1"
  Group = -> [DatumPlane002,CopyPad029001,Sketch058,Pad032]
  Origin = -> Origin040
  Placement = pos=(100,135,190) rot=(0,0,1;0rad)
  Tip = -> Pad032
FEATURE [PartDesign::ShapeBinder] CopyPocket018
  Placement = pos=(0,0,15) rot=(0,0,1;0rad)
  TraceSupport = false
FEATURE [PartDesign::Plane] DatumPlane003
  Length = 60
  MapMode = 5
  Placement = pos=(0,0,15) rot=(0,0,1;0rad)
  ResizeMode = 0
  Support = -> [CopyPocket018]
  Width = 60
FEATURE [Sketcher::SketchObject] Sketch059
  MapMode = 5
  Placement = pos=(0,0,15) rot=(0,0,1;0rad)
  Support = -> [DatumPlane003]
  sketch-geometry (21):
    g0: LineSegment StartX=-55 StartY=-21 StartZ=0 EndX=65 EndY=-21 EndZ=0
    g1: LineSegment [constr] StartX=80 StartY=-36 StartZ=0 EndX=80 EndY=-91 EndZ=0
    g2: LineSegment [constr] StartX=80 StartY=-91 StartZ=0 EndX=-70 EndY=-91 EndZ=0
    g3: LineSegment StartX=-70 StartY=-91 StartZ=0 EndX=-70 EndY=-36 EndZ=0
    g4: LineSegment StartX=-70 StartY=-91 StartZ=0 EndX=-60 EndY=-91 EndZ=0
    g5: LineSegment StartX=-60 StartY=-91 StartZ=0 EndX=-60 EndY=-82 EndZ=0
    g6: LineSegment StartX=-60 StartY=-82 StartZ=0 EndX=-40 EndY=-82 EndZ=0
    g7: LineSegment StartX=-40 StartY=-82 StartZ=0 EndX=-40 EndY=-91 EndZ=0
    g8: ArcOfCircle CenterX=-55 CenterY=-36 CenterZ=0 NormalX=0 NormalY=0 NormalZ=1 AngleXU=0 Radius=15 StartAngle=1.5708 EndAngle=3.14159
    g9: ArcOfCircle CenterX=65 CenterY=-36 CenterZ=0 NormalX=0 NormalY=0 NormalZ=1 AngleXU=0 Radius=15 StartAngle=0 EndAngle=1.5708
    g10: LineSegment StartX=80 StartY=-76 StartZ=0 EndX=71 EndY=-76 EndZ=0
    g11: LineSegment StartX=71 StartY=-76 StartZ=0 EndX=71 EndY=-61 EndZ=0
    g12: LineSegment StartX=71 StartY=-61 StartZ=0 EndX=80 EndY=-61 EndZ=0
    g13: LineSegment StartX=80 StartY=-61 StartZ=0 EndX=80 EndY=-51 EndZ=0
    g14: LineSegment StartX=80 StartY=-51 StartZ=0 EndX=71 EndY=-51 EndZ=0
    g15: LineSegment StartX=71 StartY=-51 StartZ=0 EndX=71 EndY=-36 EndZ=0
    g16: LineSegment StartX=71 StartY=-36 StartZ=0 EndX=80 EndY=-36 EndZ=0
    g17: LineSegment StartX=-40 StartY=-91 StartZ=0 EndX=50 EndY=-91 EndZ=0
    g18: LineSegment StartX=50 StartY=-91 StartZ=0 EndX=50 EndY=-82 EndZ=0
    g19: LineSegment StartX=50 StartY=-82 StartZ=0 EndX=80 EndY=-82 EndZ=0
    g20: LineSegment StartX=80 StartY=-82 StartZ=0 EndX=80 EndY=-76 EndZ=0
  constraints (60):
    c: Coincident(g1,g2)
    c: Coincident(g2,g3)
    c: Horizontal(g0)
    c: Horizontal(g2)
    c: Vertical(g1)
    c: Vertical(g3)
    c: Coincident(g3,g4)
    c: PointOnObject(g4,g2)
    c: Coincident(g4,g5)
    c: Coincident(g5,g6)
    c: Horizontal(g6)
    c: Coincident(g6,g7)
    c: PointOnObject(g7,g2)
    c: Vertical(g5)
    c: Vertical(g7)
    c: Tangent(g3,g8) = 1.5708
    c: Tangent(g0,g8) = 1.5708
    c: Tangent(g0,g9) = 1.5708
    c: Tangent(g1,g9) = 1.5708
    c: PointOnObject(g10,g1)
    c: Horizontal(g10)
    c: Coincident(g10,g11)
    c: Vertical(g11)
    c: Coincident(g11,g12)
    c: PointOnObject(g12,g1)
    c: Coincident(g12,g13)
    c: PointOnObject(g13,g1)
    c: Coincident(g13,g14)
    c: Coincident(g14,g15)
    c: Coincident(g15,g16)
    c: Horizontal(g16)
    c: Horizontal(g14)
    c: Horizontal(g12)
    c: Vertical(g15)
    c: DistanceY(g5,g5) = 9
    c: Equal(g12,g14)
    c: DistanceX(g10,g10) = 9
    c: DistanceX(g4,g4) = 10
    c: DistanceX(g6,g6) = 20
    c: DistanceY(g-1,g3) = -91
    c: Equal(g8,g9)
    c: Equal(g15,g11)
    c: Distance(g16,g13) = 15
    c: Coincident(g9,g16)
    c: Distance(g0,g2) = 70
    c: Distance(g8,g2) = 55
    c: DistanceX(g-2,g8) = -55
    c: Coincident(g7,g17)
    c: PointOnObject(g17,g2)
    c: Coincident(g17,g18)
    c: Vertical(g18)
    c: Coincident(g18,g19)
    c: Horizontal(g19)
    c: Coincident(g20,g19)
    c: Vertical(g20)
    c: DistanceX(g19,g19) = 30
    c: DistanceY(g18,g18) = 9
    c: DistanceX(g17,g17) = 90
    c: Coincident(g20,g10)
    c: DistanceY(g20,g20) = 6
FEATURE [PartDesign::Pad] Pad033
  Length = 10
  Length2 = 100
  Placement = pos=(0,0,15) rot=(0,0,1;0rad)
  Profile = -> Sketch059
  Type = 0
FEATURE [PartDesign::Body] Body033  label="Plate ganz oben"
  Group = -> [DatumPlane003,CopyPocket018,Sketch059,Pad033]
  Origin = -> Origin041
  Placement = pos=(100,135,230) rot=(0,0,1;0rad)
  Tip = -> Pad033
FEATURE [PartDesign::ShapeBinder] CopyPocket015
  Placement = pos=(0,0,0) rot=(0.57735,0.57735,0.57735;2.0944rad)
  TraceSupport = false
FEATURE [PartDesign::Plane] DatumPlane005
  Length = 60
  MapMode = 5
  Placement = pos=(80,2.6869e-12,-3.772e-13) rot=(0.57735,0.57735,0.57735;2.0944rad)
  ResizeMode = 0
  Support = -> [CopyPocket015]
  Width = 60
FEATURE [Sketcher::SketchObject] Sketch061
  MapMode = 5
  Placement = pos=(80,2.6869e-12,-3.772e-13) rot=(0.57735,0.57735,0.57735;2.0944rad)
  Support = -> [DatumPlane005]
  sketch-geometry (37):
    g0: LineSegment [constr] StartX=-91 StartY=225.5 StartZ=0 EndX=64 EndY=225.5 EndZ=0
    g1: LineSegment [constr] StartX=64 StartY=225.5 StartZ=0 EndX=64 EndY=20 EndZ=0
    g2: LineSegment [constr] StartX=64 StartY=20 StartZ=0 EndX=-91 EndY=20 EndZ=0
    g3: LineSegment [constr] StartX=-91 StartY=20 StartZ=0 EndX=-91 EndY=225.5 EndZ=0
    g4: LineSegment StartX=-62 StartY=20 StartZ=0 EndX=-62 EndY=35 EndZ=0
    g5: LineSegment StartX=-91 StartY=35 StartZ=0 EndX=-62 EndY=35 EndZ=0
    g6: LineSegment StartX=-62 StartY=20 StartZ=0 EndX=-42 EndY=20 EndZ=0
    g7: LineSegment StartX=-42 StartY=20 StartZ=0 EndX=-42 EndY=35 EndZ=0
    g8: LineSegment StartX=-42 StartY=35 StartZ=0 EndX=-32 EndY=35 EndZ=0
    g9: LineSegment StartX=-32 StartY=35 StartZ=0 EndX=-32 EndY=20 EndZ=0
    g10: LineSegment StartX=-32 StartY=20 StartZ=0 EndX=-12 EndY=20 EndZ=0
    g11: LineSegment StartX=-12 StartY=20 StartZ=0 EndX=-12 EndY=35 EndZ=0
    g12: LineSegment StartX=-12 StartY=35 StartZ=0 EndX=-2 EndY=35 EndZ=0
    g13: LineSegment StartX=-2 StartY=35 StartZ=0 EndX=-2 EndY=20 EndZ=0
    g14: LineSegment StartX=-2 StartY=20 StartZ=0 EndX=18 EndY=20 EndZ=0
    g15: LineSegment StartX=18 StartY=20 StartZ=0 EndX=18 EndY=35 EndZ=0
    g16: LineSegment StartX=18 StartY=35 StartZ=0 EndX=28 EndY=35 EndZ=0
    g17: LineSegment StartX=28 StartY=35 StartZ=0 EndX=28 EndY=20 EndZ=0
    g18: LineSegment StartX=28 StartY=20 StartZ=0 EndX=48 EndY=20 EndZ=0
    g19: LineSegment StartX=48 StartY=20 StartZ=0 EndX=48 EndY=35 EndZ=0
    g20: LineSegment StartX=48 StartY=35 StartZ=0 EndX=64 EndY=35 EndZ=0
    g21: LineSegment [constr] StartX=-91 StartY=225.5 StartZ=0 EndX=-91 EndY=35 EndZ=0
    g22: LineSegment [constr] StartX=64 StartY=35 StartZ=0 EndX=64 EndY=225.5 EndZ=0
    g23: LineSegment StartX=-91 StartY=215.5 StartZ=0 EndX=-76 EndY=215.5 EndZ=0
    g24: LineSegment StartX=-76 StartY=215.5 StartZ=0 EndX=-76 EndY=225.5 EndZ=0
    g25: LineSegment StartX=-76 StartY=225.5 StartZ=0 EndX=-61 EndY=225.5 EndZ=0
    g26: LineSegment StartX=-61 StartY=225.5 StartZ=0 EndX=-61 EndY=215.5 EndZ=0
    g27: LineSegment StartX=-61 StartY=215.5 StartZ=0 EndX=-51 EndY=215.5 EndZ=0
    g28: LineSegment StartX=-51 StartY=215.5 StartZ=0 EndX=-51 EndY=225.5 EndZ=0
    g29: LineSegment StartX=-51 StartY=225.5 StartZ=0 EndX=-36 EndY=225.5 EndZ=0
    g30: LineSegment StartX=-36 StartY=225.5 StartZ=0 EndX=-36 EndY=215.5 EndZ=0
    g31: LineSegment StartX=-36 StartY=215.5 StartZ=0 EndX=64 EndY=35 EndZ=0
    g32: LineSegment StartX=-91 StartY=35 StartZ=0 EndX=-91 EndY=95.1667 EndZ=0
    g33: LineSegment StartX=-91 StartY=95.1667 StartZ=0 EndX=-82 EndY=95.1667 EndZ=0
    g34: LineSegment StartX=-82 StartY=95.1667 StartZ=0 EndX=-82 EndY=155.333 EndZ=0
    g35: LineSegment StartX=-82 StartY=155.333 StartZ=0 EndX=-91 EndY=155.333 EndZ=0
    g36: LineSegment StartX=-91 StartY=155.333 StartZ=0 EndX=-91 EndY=215.5 EndZ=0
  constraints (110):
    c: Coincident(g0,g1)
    c: Coincident(g1,g2)
    c: Coincident(g2,g3)
    c: Coincident(g3,g0)
    c: Horizontal(g0)
    c: Horizontal(g2)
    c: Vertical(g1)
    c: Vertical(g3)
    c: PointOnObject(g4,g2)
    c: Vertical(g4)
    c: PointOnObject(g5,g3)
    c: Coincident(g5,g4)
    c: Horizontal(g5)
    c: Coincident(g4,g6)
    c: PointOnObject(g6,g2)
    c: Coincident(g6,g7)
    c: Vertical(g7)
    c: Coincident(g7,g8)
    c: Horizontal(g8)
    c: Coincident(g8,g9)
    c: PointOnObject(g9,g2)
    c: Vertical(g9)
    c: Coincident(g9,g10)
    c: PointOnObject(g10,g2)
    c: Coincident(g10,g11)
    c: Vertical(g11)
    c: Coincident(g11,g12)
    c: Coincident(g12,g13)
    c: PointOnObject(g13,g2)
    c: Coincident(g13,g14)
    c: Horizontal(g14)
    c: Coincident(g14,g15)
    c: Vertical(g15)
    c: Coincident(g15,g16)
    c: Coincident(g16,g17)
    c: PointOnObject(g17,g2)
    c: Vertical(g17)
    c: Coincident(g17,g18)
    c: Horizontal(g18)
    c: Coincident(g18,g19)
    c: Vertical(g19)
    c: Coincident(g19,g20)
    c: PointOnObject(g20,g1)
    c: Horizontal(g20)
    c: Coincident(g21,g0)
    c: Coincident(g21,g5)
    c: Coincident(g22,g20)
    c: Coincident(g22,g0)
    c: Vertical(g13)
    c: Horizontal(g12)
    c: Horizontal(g16)
    c: Equal(g17,g19)
    c: Equal(g15,g13)
    c: Equal(g9,g11)
    c: Equal(g4,g7)
    c: DistanceY(g1,g20) = 15
    c: Equal(g18,g14)
    c: Equal(g14,g10)
    c: Equal(g10,g6)
    c: Equal(g8,g12)
    c: Equal(g12,g16)
    c: DistanceX(g18,g18) = 20
    c: DistanceX(g16,g16) = 10
    c: DistanceX(g20,g20) = 16
    c: DistanceY(g1,g1) = 205.5
    c: PointOnObject(g23,g3)
    c: Horizontal(g23)
    c: Coincident(g23,g24)
    c: PointOnObject(g24,g0)
    c: Vertical(g24)
    c: Coincident(g24,g25)
    c: PointOnObject(g25,g0)
    c: Coincident(g25,g26)
    c: Vertical(g26)
    c: Coincident(g26,g27)
    c: Horizontal(g27)
    c: Coincident(g27,g28)
    c: Vertical(g28)
    c: Coincident(g28,g29)
    c: Horizontal(g29)
    c: Coincident(g29,g30)
    c: Vertical(g30)
    c: Coincident(g30,g31)
    c: Coincident(g31,g20)
    c: PointOnObject(g28,g0)
    c: DistanceY(g-1,g1) = 20
    c: Equal(g24,g26)
    c: Equal(g28,g30)
    c: DistanceY(g23,g0) = 10
    c: Equal(g25,g29)
    c: Distance(g0,g24) = 15
    c: Equal(g25,g29)
    c: Distance(g25) = 15
    c: DistanceX(g0,g0) = 155
    c: DistanceX(g-2,g2) = -91
    c: Coincident(g5,g32)
    c: PointOnObject(g32,g3)
    c: Coincident(g32,g33)
    c: Coincident(g33,g34)
    c: Vertical(g34)
    c: Coincident(g34,g35)
    c: PointOnObject(g35,g3)
    c: Horizontal(g35)
    c: Coincident(g35,g36)
    c: Coincident(g36,g23)
    c: Horizontal(g33)
    c: Equal(g36,g34)
    c: Equal(g34,g32)
    c: DistanceX(g35,g35) = 9
    c: DistanceX(g27,g27) = 10
FEATURE [PartDesign::Pad] Pad035
  Length = 9
  Length2 = 100
  Placement = pos=(80,2.6869e-12,-3.772e-13) rot=(0.57735,0.57735,0.57735;2.0944rad)
  Profile = -> Sketch061
  Reversed = true
  Type = 0
FEATURE [PartDesign::Body] Body035  label="Wand - Dreieck"
  Group = -> [DatumPlane005,CopyPocket015,Sketch061,Pad035]
  Origin = -> Origin043
  Placement = pos=(100,135,29.5) rot=(0,0,1;0rad)
  Tip = -> Pad035
FEATURE [PartDesign::ShapeBinder] CopyPad033
  Placement = pos=(0,0,15) rot=(0,0,1;0rad)
  TraceSupport = false
FEATURE [PartDesign::Plane] DatumPlane006
  Length = 60
  MapMode = 5
  Placement = pos=(0,-91,15) rot=(1,0,0;1.5708rad)
  ResizeMode = 0
  Support = -> [CopyPad033]
  Width = 60
FEATURE [Sketcher::SketchObject] Sketch062
  MapMode = 5
  Placement = pos=(0,-91,15) rot=(1,0,0;1.5708rad)
  Support = -> [DatumPlane006]
  sketch-geometry (15):
    g0: LineSegment StartX=50 StartY=10 StartZ=0 EndX=80 EndY=10 EndZ=0
    g1: LineSegment [constr] StartX=80 StartY=10 StartZ=0 EndX=80 EndY=-195.5 EndZ=0
    g2: LineSegment [constr] StartX=80 StartY=-195.5 StartZ=0 EndX=50 EndY=-195.5 EndZ=0
    g3: LineSegment [constr] StartX=50 StartY=-195.5 StartZ=0 EndX=50 EndY=10 EndZ=0
    g4: LineSegment StartX=80 StartY=10 StartZ=0 EndX=80 EndY=0 EndZ=0
    g5: LineSegment StartX=80 StartY=0 StartZ=0 EndX=71 EndY=0 EndZ=0
    g6: LineSegment StartX=71 StartY=0 StartZ=0 EndX=71 EndY=-60 EndZ=0
    g7: LineSegment StartX=71 StartY=-60 StartZ=0 EndX=80 EndY=-60 EndZ=0
    g8: LineSegment StartX=80 StartY=-60 StartZ=0 EndX=80 EndY=-120 EndZ=0
    g9: LineSegment StartX=80 StartY=-120 StartZ=0 EndX=71 EndY=-120 EndZ=0
    g10: LineSegment StartX=71 StartY=-120 StartZ=0 EndX=71 EndY=-195.5 EndZ=0
    g11: LineSegment StartX=71 StartY=-195.5 StartZ=0 EndX=61 EndY=-195.5 EndZ=0
    g12: LineSegment StartX=61 StartY=-195.5 StartZ=0 EndX=61 EndY=-180.5 EndZ=0
    g13: LineSegment StartX=61 StartY=-180.5 StartZ=0 EndX=50 EndY=-180.5 EndZ=0
    g14: LineSegment StartX=50 StartY=-180.5 StartZ=0 EndX=50 EndY=10 EndZ=0
  constraints (44):
    c: Coincident(g0,g1)
    c: Coincident(g1,g2)
    c: Coincident(g2,g3)
    c: Coincident(g3,g0)
    c: Horizontal(g0)
    c: Horizontal(g2)
    c: Vertical(g1)
    c: Vertical(g3)
    c: DistanceX(g0,g0) = 30
    c: Coincident(g0,g4)
    c: PointOnObject(g4,g1)
    c: Coincident(g4,g5)
    c: Horizontal(g5)
    c: Coincident(g5,g6)
    c: Vertical(g6)
    c: Coincident(g6,g7)
    c: Horizontal(g7)
    c: Coincident(g7,g8)
    c: Vertical(g8)
    c: Coincident(g8,g9)
    c: Coincident(g9,g10)
    c: Vertical(g10)
    c: Horizontal(g9)
    c: Equal(g9,g7)
    c: Equal(g5,g7)
    c: DistanceY(g3,g3) = 205.5
    c: DistanceY(g-1,g0) = 10
    c: DistanceX(g-2,g0) = 80
    c: DistanceX(g5,g5) = 9
    c: Equal(g8,g6)
    c: DistanceY(g4,g4) = 10
    c: PointOnObject(g10,g2)
    c: Coincident(g10,g11)
    c: PointOnObject(g11,g2)
    c: Coincident(g11,g12)
    c: Coincident(g12,g13)
    c: PointOnObject(g13,g3)
    c: Horizontal(g13)
    c: Coincident(g14,g13)
    c: Coincident(g14,g0)
    c: Vertical(g12)
    c: DistanceY(g12,g12) = 15
    c: DistanceY(g6,g6) = 60
    c: DistanceX(g11,g11) = 10
FEATURE [PartDesign::Pad] Pad036
  Length = 9
  Length2 = 100
  Placement = pos=(0,-91,15) rot=(1,0,0;1.5708rad)
  Profile = -> Sketch062
  Reversed = true
  Type = 0
FEATURE [PartDesign::Body] Body036  label="Wand f Platte oben 1"
  Group = -> [DatumPlane006,CopyPad033,Sketch062,Pad036]
  Origin = -> Origin044
  Placement = pos=(100,135,230) rot=(0,0,1;0rad)
  Tip = -> Pad036
FEATURE [PartDesign::ShapeBinder] CopyPad033001
  Placement = pos=(0,0,15) rot=(0,0,1;0rad)
  TraceSupport = false
FEATURE [PartDesign::Plane] DatumPlane007
  Length = 60
  MapMode = 5
  Placement = pos=(0,-91,15) rot=(1,0,0;1.5708rad)
  ResizeMode = 0
  Support = -> [CopyPad033001]
  Width = 60
FEATURE [Sketcher::SketchObject] Sketch063
  MapMode = 5
  Placement = pos=(0,-91,15) rot=(1,0,0;1.5708rad)
  Support = -> [DatumPlane007]
  sketch-geometry (16):
    g0: LineSegment [constr] StartX=-70 StartY=10 StartZ=0 EndX=-30 EndY=10 EndZ=0
    g1: LineSegment [constr] StartX=-30 StartY=10 StartZ=0 EndX=-30 EndY=-195.5 EndZ=0
    g2: LineSegment [constr] StartX=-30 StartY=-195.5 StartZ=0 EndX=-70 EndY=-195.5 EndZ=0
    g3: LineSegment [constr] StartX=-70 StartY=-195.5 StartZ=0 EndX=-70 EndY=10 EndZ=0
    g4: LineSegment StartX=-70 StartY=-180.5 StartZ=0 EndX=-60 EndY=-180.5 EndZ=0
    g5: LineSegment StartX=-60 StartY=-180.5 StartZ=0 EndX=-60 EndY=-195.5 EndZ=0
    g6: LineSegment StartX=-60 StartY=-195.5 StartZ=0 EndX=-40 EndY=-195.5 EndZ=0
    g7: LineSegment StartX=-40 StartY=-195.5 StartZ=0 EndX=-40 EndY=-180.5 EndZ=0
    g8: LineSegment StartX=-40 StartY=-180.5 StartZ=0 EndX=-30 EndY=-180.5 EndZ=0
    g9: LineSegment StartX=-30 StartY=-180.5 StartZ=0 EndX=-30 EndY=0 EndZ=0
    g10: LineSegment StartX=-30 StartY=0 StartZ=0 EndX=-40 EndY=0 EndZ=0
    g11: LineSegment StartX=-40 StartY=0 StartZ=0 EndX=-40 EndY=10 EndZ=0
    g12: LineSegment StartX=-40 StartY=10 StartZ=0 EndX=-60 EndY=10 EndZ=0
    g13: LineSegment StartX=-60 StartY=10 StartZ=0 EndX=-60 EndY=0 EndZ=0
    g14: LineSegment StartX=-60 StartY=0 StartZ=0 EndX=-70 EndY=0 EndZ=0
    g15: LineSegment StartX=-70 StartY=0 StartZ=0 EndX=-70 EndY=-180.5 EndZ=0
  constraints (48):
    c: Coincident(g0,g1)
    c: Coincident(g1,g2)
    c: Coincident(g2,g3)
    c: Coincident(g3,g0)
    c: Horizontal(g0)
    c: Horizontal(g2)
    c: Vertical(g1)
    c: Vertical(g3)
    c: PointOnObject(g4,g3)
    c: Horizontal(g4)
    c: Coincident(g4,g5)
    c: PointOnObject(g5,g2)
    c: Coincident(g5,g6)
    c: PointOnObject(g6,g2)
    c: Coincident(g6,g7)
    c: Coincident(g7,g8)
    c: PointOnObject(g8,g1)
    c: Horizontal(g8)
    c: Coincident(g8,g9)
    c: PointOnObject(g9,g-1)
    c: Vertical(g9)
    c: Coincident(g9,g10)
    c: Horizontal(g10)
    c: Coincident(g10,g11)
    c: PointOnObject(g11,g0)
    c: Vertical(g11)
    c: Coincident(g11,g12)
    c: PointOnObject(g12,g0)
    c: Coincident(g12,g13)
    c: PointOnObject(g13,g-1)
    c: Vertical(g13)
    c: Coincident(g13,g14)
    c: PointOnObject(g14,g-1)
    c: Coincident(g14,g15)
    c: Coincident(g15,g4)
    c: Vertical(g15)
    c: Vertical(g5)
    c: Vertical(g7)
    c: Distance(g12,g3) = 10
    c: Distance(g14,g0) = 10
    c: Distance(g2,g4) = 15
    c: Equal(g5,g7)
    c: DistanceX(g6,g6) = 20
    c: DistanceX(g12,g12) = 20
    c: DistanceX(g-2,g0) = -30
    c: DistanceY(g15,g15) = 180.5
    c: DistanceX(g11,g0) = 10
    c: Equal(g4,g8)
FEATURE [PartDesign::Pad] Pad037
  Length = 9
  Length2 = 100
  Placement = pos=(0,-91,15) rot=(1,0,0;1.5708rad)
  Profile = -> Sketch063
  Reversed = true
  Type = 0
FEATURE [PartDesign::Body] Body037  label="Wand für Platte oben 2"
  Group = -> [DatumPlane007,CopyPad033001,Sketch063,Pad037]
  Origin = -> Origin045
  Placement = pos=(100,135,230) rot=(0,0,1;0rad)
  Tip = -> Pad037
FEATURE [PartDesign::CoordinateSystem] LCS_1005
  AttacherType = Attacher::AttachEngine3D
  MapMode = 2
  Support = -> [X_Axis046]
FEATURE [App::Part] Aufbau_Tisch
  Group = -> [LCS_1005,Body029,Body030,Body032,Body033,Body035,Body036,Body037,Body031]
  Origin = -> Origin046
FEATURE [App::Part] Model
  Group = -> [LCS_0,Constraints,Variables,fuehrung_horiz_gewinde,dosierer,motor_kasten_horiz,glas,motoren,Aufbau_Tisch]
  Origin = -> Origin032
